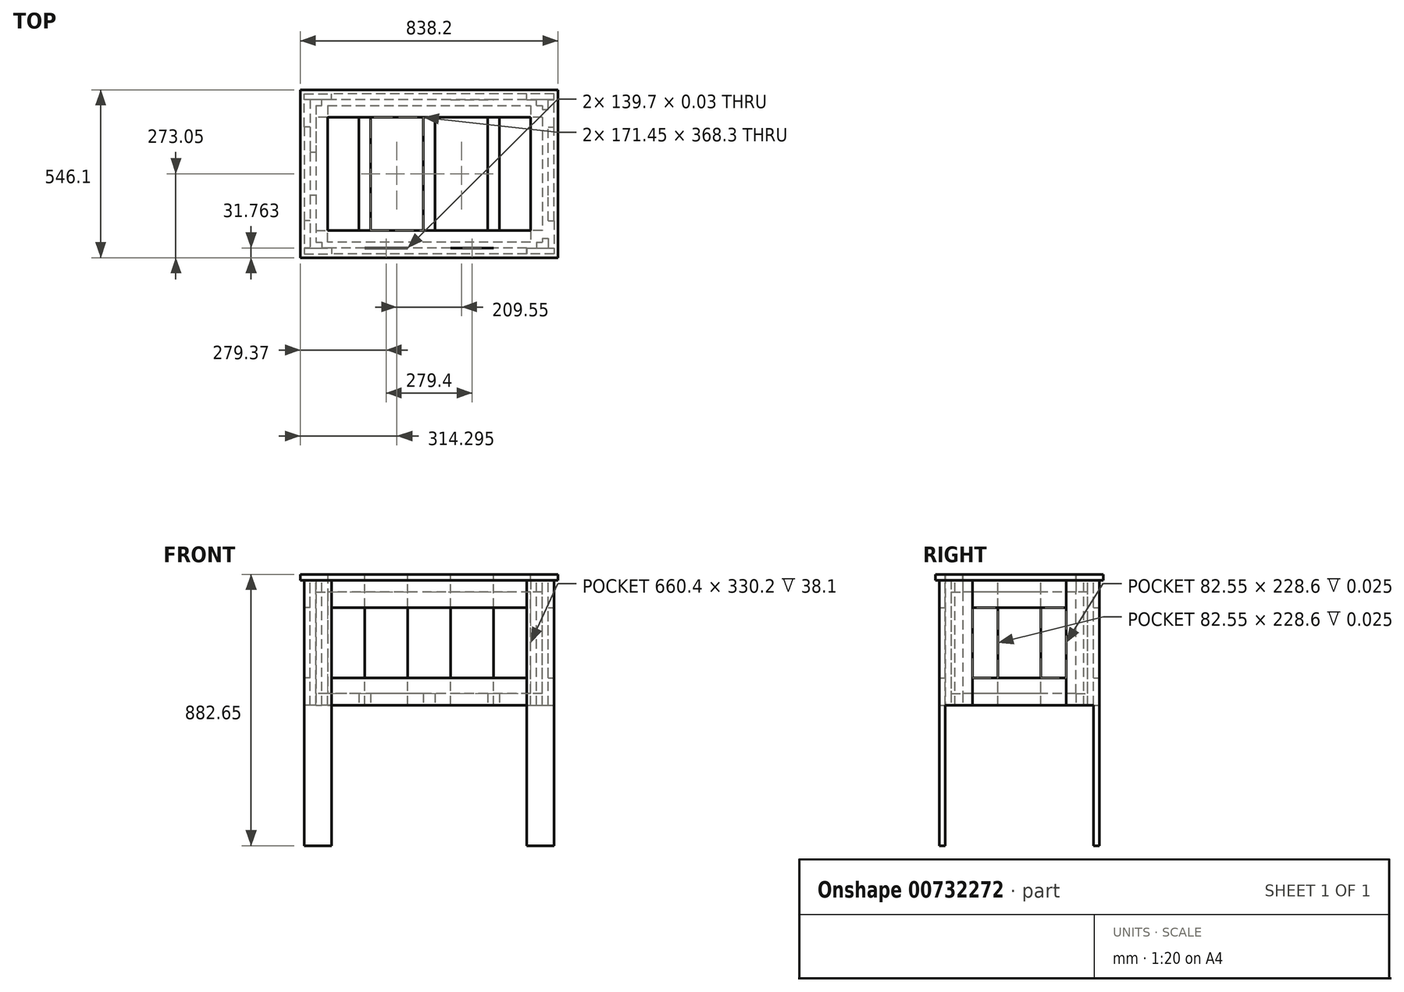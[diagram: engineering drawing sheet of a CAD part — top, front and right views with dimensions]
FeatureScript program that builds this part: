
annotation { "Feature Type Name" : "Feature", "Feature Type Description" : "" }
export const myFeature = defineFeature(function(context is Context, id is Id, definition is map)
    precondition{}
    {
        {
            var Q0;
            Q0=qCreatedBy(makeId("Top.planeOp"),FACE);
            var sketch = newSketch(context, id + "F0", { "sketchPlane" : qUnion([Q0])});
            skLineSegment(sketch, "E0.bottom", {"start": v(0, 0) * mm, "end": v(38.1, 0) * mm});
            skLineSegment(sketch, "E0.top", {"start": v(0, -38.1) * mm, "end": v(38.1, -38.1) * mm});
            skLineSegment(sketch, "E0.left", {"start": v(0, 0) * mm, "end": v(0, -38.1) * mm});
            skLineSegment(sketch, "E0.right", {"start": v(38.1, 0) * mm, "end": v(38.1, -38.1) * mm});
            skSolve(sketch);
        }
        {
            var Q0;
            Q0 = qSketchRegion(id + "F0", true);
            extrude(context, id + "F1", {"entities" : qUnion([Q0]), "depth" : 406.4 * mm, "offsetDistance" : 25.4 * mm});
        }
        {
            var Q0;
            Q0=makeQuery(id+"F1.opExtrude","SWEPT_FACE",FACE,{"disambiguationData":[OSD([sQuery(id+"F0.wireOp",EDGE,"E0.right")])]});
            var sketch = newSketch(context, id + "F2", { "sketchPlane" : qUnion([Q0])});
            skLineSegment(sketch, "E1.bottom", {"start": v(-38.1, 406.4) * mm, "end": v(0, 406.4) * mm});
            skLineSegment(sketch, "E1.top", {"start": v(-38.1, 368.3) * mm, "end": v(0, 368.3) * mm});
            skLineSegment(sketch, "E1.left", {"start": v(-38.1, 406.4) * mm, "end": v(-38.1, 368.3) * mm});
            skLineSegment(sketch, "E1.right", {"start": v(0, 406.4) * mm, "end": v(0, 368.3) * mm});
            skSolve(sketch);
        }
        {
            var Q0;
            Q0=makeQuery(id+"F2.imprint","IMPRINT",FACE,{"disambiguationData":[TD([[makeQuery(id+"F2.imprint","IMPRINT",EDGE,{"derivedFrom":sQuery(id+"F2.wireOp",EDGE,"E1.bottom")}),1.0]])]});
            var sketch = newSketch(context, id + "F3", { "sketchPlane" : qUnion([Q0])});
            skSolve(sketch);
        }
        {
            var Q0;
            Q0=makeQuery(id+"F3.imprint","IMPRINT",FACE,{"disambiguationData":[TD([[makeQuery(id+"F3.imprint","IMPRINT",EDGE,{"derivedFrom":makeQuery(id+"F2.imprint","IMPRINT",EDGE,{"derivedFrom":sQuery(id+"F2.wireOp",EDGE,"E1.bottom")})}),1.0]])]});
            extrude(context, id + "F4", {"entities" : qUnion([Q0]), "operationType" : NewBodyOperationType.ADD, "depth" : 660.4 * mm, "offsetDistance" : 25.4 * mm});
        }
        {
            var Q0;
            Q0=makeQuery(id+"F4.boolean.opBoolean","MERGE",FACE,{"derivedFrom":[makeQuery(id+"F1.opExtrude","CAP_FACE",FACE,{"disambiguationData":[OSD([sQuery(id+"F0.wireOp",EDGE,"E0.bottom"),sQuery(id+"F0.wireOp",EDGE,"E0.top"),sQuery(id+"F0.wireOp",EDGE,"E0.left"),sQuery(id+"F0.wireOp",EDGE,"E0.right")])],"isStart":false}),makeQuery(id+"F4.opExtrude","SWEPT_FACE",FACE,{"disambiguationData":[OSD([sQuery(id+"F2.wireOp",EDGE,"E1.bottom")])]})]});
            var sketch = newSketch(context, id + "F5", { "sketchPlane" : qUnion([Q0])});
            skLineSegment(sketch, "E2.bottom", {"start": v(698.5, 0) * mm, "end": v(736.6, 0) * mm});
            skLineSegment(sketch, "E2.top", {"start": v(698.5, -38.1) * mm, "end": v(736.6, -38.1) * mm});
            skLineSegment(sketch, "E2.left", {"start": v(698.5, 0) * mm, "end": v(698.5, -38.1) * mm});
            skLineSegment(sketch, "E2.right", {"start": v(736.6, 0) * mm, "end": v(736.6, -38.1) * mm});
            skSolve(sketch);
        }
        {
            var Q0;
            Q0=makeQuery(id+"F5.imprint","IMPRINT",FACE,{"disambiguationData":[TD([[makeQuery(id+"F5.imprint","IMPRINT",EDGE,{"derivedFrom":sQuery(id+"F5.wireOp",EDGE,"E2.bottom")}),-1.0]])]});
            extrude(context, id + "F6", {"entities" : qUnion([Q0]), "operationType" : NewBodyOperationType.ADD, "oppositeDirection" : true, "depth" : 406.4 * mm, "offsetDistance" : 25.4 * mm});
        }
        {
            var Q0;
            Q0 = qSketchRegion(id + "F2", true);
            var sketch = newSketch(context, id + "F7", { "sketchPlane" : qUnion([Q0])});
            skLineSegment(sketch, "E3.bottom", {"start": v(-38.1, 0) * mm, "end": v(0, 0) * mm});
            skLineSegment(sketch, "E3.top", {"start": v(-38.1, 38.1) * mm, "end": v(0, 38.1) * mm});
            skLineSegment(sketch, "E3.left", {"start": v(-38.1, 0) * mm, "end": v(-38.1, 38.1) * mm});
            skLineSegment(sketch, "E3.right", {"start": v(0, 0) * mm, "end": v(0, 38.1) * mm});
            skSolve(sketch);
        }
        {
            var Q0;
            Q0=makeQuery(id+"F7.imprint","IMPRINT",FACE,{"disambiguationData":[TD([[makeQuery(id+"F7.imprint","IMPRINT",EDGE,{"derivedFrom":sQuery(id+"F7.wireOp",EDGE,"E3.bottom")}),1.0]])]});
            extrude(context, id + "F8", {"entities" : qUnion([Q0]), "operationType" : NewBodyOperationType.ADD, "endBound" : BoundingType.UP_TO_NEXT, "depth" : 25.4 * mm, "offsetDistance" : 25.4 * mm});
        }
        {
            var Q0;
            Q0=makeQuery(id+"F8.boolean.opBoolean","MERGE",FACE,{"derivedFrom":[makeQuery(id+"F6.boolean.opBoolean","MERGE",FACE,{"derivedFrom":[makeQuery(id+"F4.boolean.opBoolean","MERGE",FACE,{"derivedFrom":[makeQuery(id+"F1.opExtrude","SWEPT_FACE",FACE,{"disambiguationData":[OSD([sQuery(id+"F0.wireOp",EDGE,"E0.bottom")])]}),makeQuery(id+"F4.opExtrude","SWEPT_FACE",FACE,{"disambiguationData":[OSD([sQuery(id+"F2.wireOp",EDGE,"E1.right")])]})]}),makeQuery(id+"F6.opExtrude","SWEPT_FACE",FACE,{"disambiguationData":[OSD([sQuery(id+"F5.wireOp",EDGE,"E2.bottom")])]})]}),makeQuery(id+"F8.opExtrude","SWEPT_FACE",FACE,{"disambiguationData":[OSD([sQuery(id+"F7.wireOp",EDGE,"E3.right")])]})]});
            var sketch = newSketch(context, id + "F9", { "sketchPlane" : qUnion([Q0])});
            skLineSegment(sketch, "E4.bottom", {"start": v(-736.6, 406.4) * mm, "end": v(-698.5, 406.4) * mm});
            skLineSegment(sketch, "E4.top", {"start": v(-736.6, 368.3) * mm, "end": v(-698.5, 368.3) * mm});
            skLineSegment(sketch, "E4.left", {"start": v(-736.6, 406.4) * mm, "end": v(-736.6, 368.3) * mm});
            skLineSegment(sketch, "E4.right", {"start": v(-698.5, 406.4) * mm, "end": v(-698.5, 368.3) * mm});
            skLineSegment(sketch, "E5.bottom", {"start": v(-736.6, 0) * mm, "end": v(-698.5, 0) * mm});
            skLineSegment(sketch, "E5.top", {"start": v(-736.6, 38.1) * mm, "end": v(-698.5, 38.1) * mm});
            skLineSegment(sketch, "E5.left", {"start": v(-736.6, 0) * mm, "end": v(-736.6, 38.1) * mm});
            skLineSegment(sketch, "E5.right", {"start": v(-698.5, 0) * mm, "end": v(-698.5, 38.1) * mm});
            skLineSegment(sketch, "E6.bottom", {"start": v(-698.5, 38.1) * mm, "end": v(-698.5, 38.1) * mm});
            skLineSegment(sketch, "E6.top", {"start": v(-698.5, 38.1) * mm, "end": v(-698.5, 38.1) * mm});
            skLineSegment(sketch, "E6.left", {"start": v(-698.5, 38.1) * mm, "end": v(-698.5, 38.1) * mm});
            skLineSegment(sketch, "E6.right", {"start": v(-698.5, 38.1) * mm, "end": v(-698.5, 38.1) * mm});
            skLineSegment(sketch, "E7.bottom", {"start": v(0, 406.4) * mm, "end": v(-38.1, 406.4) * mm});
            skLineSegment(sketch, "E7.top", {"start": v(0, 368.3) * mm, "end": v(-38.1, 368.3) * mm});
            skLineSegment(sketch, "E7.left", {"start": v(0, 406.4) * mm, "end": v(0, 368.3) * mm});
            skLineSegment(sketch, "E7.right", {"start": v(-38.1, 406.4) * mm, "end": v(-38.1, 368.3) * mm});
            skLineSegment(sketch, "E8.bottom", {"start": v(0, 0) * mm, "end": v(-38.1, 0) * mm});
            skLineSegment(sketch, "E8.top", {"start": v(0, 38.1) * mm, "end": v(-38.1, 38.1) * mm});
            skLineSegment(sketch, "E8.left", {"start": v(0, 0) * mm, "end": v(0, 38.1) * mm});
            skLineSegment(sketch, "E8.right", {"start": v(-38.1, 0) * mm, "end": v(-38.1, 38.1) * mm});
            skSolve(sketch);
        }
        {
            var Q0;
            Q0=makeQuery(id+"F9.imprint","IMPRINT",FACE,{"disambiguationData":[TD([[makeQuery(id+"F9.imprint","IMPRINT",EDGE,{"derivedFrom":sQuery(id+"F9.wireOp",EDGE,"E4.bottom")}),1.0]])]});
            var Q1;
            Q1=makeQuery(id+"F9.imprint","IMPRINT",FACE,{"disambiguationData":[TD([[makeQuery(id+"F9.imprint","IMPRINT",EDGE,{"derivedFrom":sQuery(id+"F9.wireOp",EDGE,"E5.bottom")}),-1.0]])]});
            var Q2;
            Q2=makeQuery(id+"F9.imprint","IMPRINT",FACE,{"disambiguationData":[TD([[makeQuery(id+"F9.imprint","IMPRINT",EDGE,{"derivedFrom":sQuery(id+"F9.wireOp",EDGE,"E8.bottom")}),-1.0]])]});
            var Q3;
            Q3=makeQuery(id+"F9.imprint","IMPRINT",FACE,{"disambiguationData":[TD([[makeQuery(id+"F9.imprint","IMPRINT",EDGE,{"derivedFrom":sQuery(id+"F9.wireOp",EDGE,"E7.bottom")}),1.0]])]});
            extrude(context, id + "F10", {"entities" : qUnion([Q0, Q1, Q2, Q3]), "operationType" : NewBodyOperationType.ADD, "depth" : 368.3 * mm, "offsetDistance" : 25.4 * mm});
        }
        {
            var Q0;
            Q0=makeQuery(id+"F10.boolean.opBoolean","MERGE",FACE,{"derivedFrom":[makeQuery(id+"F6.opExtrude","SWEPT_FACE",FACE,{"disambiguationData":[OSD([sQuery(id+"F5.wireOp",EDGE,"E2.right")])]}),makeQuery(id+"F10.opExtrude","SWEPT_FACE",FACE,{"disambiguationData":[OSD([sQuery(id+"F9.wireOp",EDGE,"E4.left")])]}),makeQuery(id+"F10.opExtrude","SWEPT_FACE",FACE,{"disambiguationData":[OSD([sQuery(id+"F9.wireOp",EDGE,"E5.left")])]})]});
            var sketch = newSketch(context, id + "F11", { "sketchPlane" : qUnion([Q0])});
            skLineSegment(sketch, "E9.bottom", {"start": v(368.3, 406.4) * mm, "end": v(406.4, 406.4) * mm});
            skLineSegment(sketch, "E9.top", {"start": v(368.3, 368.3) * mm, "end": v(406.4, 368.3) * mm});
            skLineSegment(sketch, "E9.left", {"start": v(368.3, 406.4) * mm, "end": v(368.3, 368.3) * mm});
            skLineSegment(sketch, "E9.right", {"start": v(406.4, 406.4) * mm, "end": v(406.4, 368.3) * mm});
            skLineSegment(sketch, "E10.bottom", {"start": v(368.3, 38.1) * mm, "end": v(406.4, 38.1) * mm});
            skLineSegment(sketch, "E10.top", {"start": v(368.3, 0) * mm, "end": v(406.4, 0) * mm});
            skLineSegment(sketch, "E10.left", {"start": v(368.3, 38.1) * mm, "end": v(368.3, 0) * mm});
            skLineSegment(sketch, "E10.right", {"start": v(406.4, 38.1) * mm, "end": v(406.4, 0) * mm});
            skSolve(sketch);
        }
        {
            var Q0;
            Q0 = qSketchRegion(id + "F11", true);
            var Q1;
            Q1=makeQuery(id+"F11.imprint","IMPRINT",FACE,{"disambiguationData":[TD([[makeQuery(id+"F11.imprint","IMPRINT",EDGE,{"derivedFrom":sQuery(id+"F11.wireOp",EDGE,"E9.bottom")}),-1.0]])]});
            var Q2;
            Q2=makeQuery(id+"F11.imprint","IMPRINT",FACE,{"disambiguationData":[TD([[makeQuery(id+"F11.imprint","IMPRINT",EDGE,{"derivedFrom":sQuery(id+"F11.wireOp",EDGE,"E10.bottom")}),-1.0]])]});
            extrude(context, id + "F12", {"entities" : qUnion([Q0, Q1, Q2]), "operationType" : NewBodyOperationType.ADD, "oppositeDirection" : true, "depth" : 736.6 * mm, "offsetDistance" : 25.4 * mm});
        }
        {
            var Q0;
            Q0=makeQuery(id+"F12.boolean.opBoolean","MERGE",FACE,{"derivedFrom":[makeQuery(id+"F10.opExtrude","SWEPT_FACE",FACE,{"disambiguationData":[OSD([sQuery(id+"F9.wireOp",EDGE,"E4.top")])]}),makeQuery(id+"F10.opExtrude","SWEPT_FACE",FACE,{"disambiguationData":[OSD([sQuery(id+"F9.wireOp",EDGE,"E7.top")])]}),makeQuery(id+"F12.opExtrude","SWEPT_FACE",FACE,{"disambiguationData":[OSD([sQuery(id+"F11.wireOp",EDGE,"E9.top")])]})]});
            var sketch = newSketch(context, id + "F13", { "sketchPlane" : qUnion([Q0])});
            skLineSegment(sketch, "E11.bottom", {"start": v(736.6, -406.4) * mm, "end": v(698.5, -406.4) * mm});
            skLineSegment(sketch, "E11.top", {"start": v(736.6, -368.3) * mm, "end": v(698.5, -368.3) * mm});
            skLineSegment(sketch, "E11.left", {"start": v(736.6, -406.4) * mm, "end": v(736.6, -368.3) * mm});
            skLineSegment(sketch, "E11.right", {"start": v(698.5, -406.4) * mm, "end": v(698.5, -368.3) * mm});
            skLineSegment(sketch, "E12.bottom", {"start": v(0, -406.4) * mm, "end": v(38.1, -406.4) * mm});
            skLineSegment(sketch, "E12.top", {"start": v(0, -368.3) * mm, "end": v(38.1, -368.3) * mm});
            skLineSegment(sketch, "E12.left", {"start": v(0, -406.4) * mm, "end": v(0, -368.3) * mm});
            skLineSegment(sketch, "E12.right", {"start": v(38.1, -406.4) * mm, "end": v(38.1, -368.3) * mm});
            skSolve(sketch);
        }
        {
            var Q0;
            Q0=makeQuery(id+"F13.imprint","IMPRINT",FACE,{"disambiguationData":[TD([[makeQuery(id+"F13.imprint","IMPRINT",EDGE,{"derivedFrom":sQuery(id+"F13.wireOp",EDGE,"E11.bottom")}),1.0]])]});
            var Q1;
            Q1 = qSketchRegion(id + "F13", true);
            var Q2;
            Q2=makeQuery(id+"F13.imprint","IMPRINT",FACE,{"disambiguationData":[TD([[makeQuery(id+"F13.imprint","IMPRINT",EDGE,{"derivedFrom":sQuery(id+"F13.wireOp",EDGE,"E12.bottom")}),1.0]])]});
            extrude(context, id + "F14", {"entities" : qUnion([Q0, Q1, Q2]), "operationType" : NewBodyOperationType.ADD, "endBound" : BoundingType.UP_TO_NEXT, "depth" : 25.4 * mm, "offsetDistance" : 25.4 * mm});
        }
        {
            var Q0;
            {var subQ0=makeQuery(id+"F8.opExtrude","SWEPT_FACE",FACE,{"disambiguationData":[OSD([sQuery(id+"F7.wireOp",EDGE,"E3.right")])]});var subQ3=sQuery(id+"F0.wireOp",EDGE,"E0.bottom");var subQ4=makeQuery(id+"F1.opExtrude","SWEPT_FACE",FACE,{"disambiguationData":[OSD([subQ3])]});var subQ5=sQuery(id+"F5.wireOp",EDGE,"E2.bottom");var subQ6=makeQuery(id+"F6.opExtrude","SWEPT_FACE",FACE,{"disambiguationData":[OSD([subQ5])]});var subQ7=makeQuery(id+"F4.opExtrude","SWEPT_FACE",FACE,{"disambiguationData":[OSD([sQuery(id+"F2.wireOp",EDGE,"E1.right")])]});Q0=makeQuery(id+"F10.boolean.opBoolean","SPLIT",FACE,{"disambiguationData":[TD([makeQuery(id+"F8.opExtrude","SWEPT_FACE",FACE,{"disambiguationData":[OSD([sQuery(id+"F7.wireOp",EDGE,"E3.bottom")])]})])],"derivedFrom":makeQuery(id+"F8.boolean.opBoolean","MERGE",FACE,{"derivedFrom":[makeQuery(id+"F6.boolean.opBoolean","MERGE",FACE,{"derivedFrom":[makeQuery(id+"F4.boolean.opBoolean","MERGE",FACE,{"derivedFrom":[subQ4,subQ7]}),subQ6]}),subQ0]})});}
            var sketch = newSketch(context, id + "F15", { "sketchPlane" : qUnion([Q0])});
            skLineSegment(sketch, "E13.bottom", {"start": v(-596.9, 38.1) * mm, "end": v(-558.8, 38.1) * mm});
            skLineSegment(sketch, "E13.top", {"start": v(-596.9, 0) * mm, "end": v(-558.8, 0) * mm});
            skLineSegment(sketch, "E13.left", {"start": v(-596.9, 38.1) * mm, "end": v(-596.9, 0) * mm});
            skLineSegment(sketch, "E13.right", {"start": v(-558.8, 38.1) * mm, "end": v(-558.8, 0) * mm});
            skLineSegment(sketch, "E14.bottom", {"start": v(-387.35, 38.1) * mm, "end": v(-349.25, 38.1) * mm});
            skLineSegment(sketch, "E14.top", {"start": v(-387.35, -0.88) * mm, "end": v(-349.25, -0.88) * mm});
            skLineSegment(sketch, "E14.left", {"start": v(-387.35, 38.1) * mm, "end": v(-387.35, -0.88) * mm});
            skLineSegment(sketch, "E14.right", {"start": v(-349.25, 38.1) * mm, "end": v(-349.25, -0.88) * mm});
            skLineSegment(sketch, "E15.bottom", {"start": v(-177.8, 38.1) * mm, "end": v(-139.7, 38.1) * mm});
            skLineSegment(sketch, "E15.top", {"start": v(-177.8, 0) * mm, "end": v(-139.7, 0) * mm});
            skLineSegment(sketch, "E15.left", {"start": v(-177.8, 38.1) * mm, "end": v(-177.8, 0) * mm});
            skLineSegment(sketch, "E15.right", {"start": v(-139.7, 38.1) * mm, "end": v(-139.7, 0) * mm});
            skSolve(sketch);
        }
        {
            var Q0;
            Q0=makeQuery(id+"F15.imprint","IMPRINT",FACE,{"disambiguationData":[TD([[makeQuery(id+"F15.imprint","IMPRINT",EDGE,{"derivedFrom":sQuery(id+"F15.wireOp",EDGE,"E13.bottom")}),-1.0]])]});
            var Q1;
            {var subQ0=sQuery(id+"F15.wireOp",EDGE,"E14.bottom");Q1=makeQuery(id+"F15.imprint","IMPRINT",FACE,{"disambiguationData":[TD([[makeQuery(id+"F15.imprint","IMPRINT",EDGE,{"derivedFrom":subQ0}),-1.0]])]});}
            var Q2;
            Q2=makeQuery(id+"F15.imprint","IMPRINT",FACE,{"disambiguationData":[TD([[makeQuery(id+"F15.imprint","IMPRINT",EDGE,{"derivedFrom":sQuery(id+"F15.wireOp",EDGE,"E15.bottom")}),-1.0]])]});
            extrude(context, id + "F16", {"entities" : qUnion([Q0, Q1, Q2]), "operationType" : NewBodyOperationType.ADD, "endBound" : BoundingType.UP_TO_NEXT, "depth" : 25.4 * mm, "offsetDistance" : 25.4 * mm});
        }
        {
            var Q0;
            Q0=makeQuery(id+"F12.boolean.opBoolean","MERGE",FACE,{"derivedFrom":[makeQuery(id+"F10.boolean.opBoolean","MERGE",FACE,{"derivedFrom":[makeQuery(id+"F6.boolean.opBoolean","MERGE",FACE,{"derivedFrom":[makeQuery(id+"F4.boolean.opBoolean","MERGE",FACE,{"derivedFrom":[makeQuery(id+"F1.opExtrude","CAP_FACE",FACE,{"disambiguationData":[OSD([sQuery(id+"F0.wireOp",EDGE,"E0.bottom"),sQuery(id+"F0.wireOp",EDGE,"E0.top"),sQuery(id+"F0.wireOp",EDGE,"E0.left"),sQuery(id+"F0.wireOp",EDGE,"E0.right")])],"isStart":false}),makeQuery(id+"F4.opExtrude","SWEPT_FACE",FACE,{"disambiguationData":[OSD([sQuery(id+"F2.wireOp",EDGE,"E1.bottom")])]})]}),makeQuery(id+"F6.opExtrude","CAP_FACE",FACE,{"disambiguationData":[OSD([sQuery(id+"F5.wireOp",EDGE,"E2.bottom"),sQuery(id+"F5.wireOp",EDGE,"E2.top"),sQuery(id+"F5.wireOp",EDGE,"E2.left"),sQuery(id+"F5.wireOp",EDGE,"E2.right")])],"isStart":true})]}),makeQuery(id+"F10.opExtrude","SWEPT_FACE",FACE,{"disambiguationData":[OSD([sQuery(id+"F9.wireOp",EDGE,"E4.bottom")])]}),makeQuery(id+"F10.opExtrude","SWEPT_FACE",FACE,{"disambiguationData":[OSD([sQuery(id+"F9.wireOp",EDGE,"E7.bottom")])]})]}),makeQuery(id+"F12.opExtrude","SWEPT_FACE",FACE,{"disambiguationData":[OSD([sQuery(id+"F11.wireOp",EDGE,"E9.bottom")])]})]});
            var sketch = newSketch(context, id + "F17", { "sketchPlane" : qUnion([Q0])});
            skLineSegment(sketch, "E16.bottom", {"start": v(298.45, -38.1) * mm, "end": v(438.15, -38.1) * mm});
            skLineSegment(sketch, "E16.top", {"start": v(298.45, -57.15) * mm, "end": v(438.15, -57.15) * mm});
            skLineSegment(sketch, "E16.left", {"start": v(298.45, -38.1) * mm, "end": v(298.45, -57.15) * mm});
            skLineSegment(sketch, "E16.right", {"start": v(438.15, -38.1) * mm, "end": v(438.15, -57.15) * mm});
            skSolve(sketch);
        }
        {
            var Q0;
            Q0=makeQuery(id+"F17.imprint","IMPRINT",FACE,{"disambiguationData":[TD([[makeQuery(id+"F17.imprint","IMPRINT",EDGE,{"derivedFrom":sQuery(id+"F17.wireOp",EDGE,"E16.bottom")}),-1.0]])]});
            extrude(context, id + "F18", {"entities" : qUnion([Q0]), "operationType" : NewBodyOperationType.ADD, "oppositeDirection" : true, "depth" : 406.4 * mm, "offsetDistance" : 25.4 * mm});
        }
        {
            var Q0;
            Q0=makeQuery(id+"F18.boolean.opBoolean","MERGE",FACE,{"derivedFrom":[makeQuery(id+"F12.boolean.opBoolean","MERGE",FACE,{"derivedFrom":[makeQuery(id+"F10.boolean.opBoolean","MERGE",FACE,{"derivedFrom":[makeQuery(id+"F6.boolean.opBoolean","MERGE",FACE,{"derivedFrom":[makeQuery(id+"F4.boolean.opBoolean","MERGE",FACE,{"derivedFrom":[makeQuery(id+"F1.opExtrude","CAP_FACE",FACE,{"disambiguationData":[OSD([sQuery(id+"F0.wireOp",EDGE,"E0.bottom"),sQuery(id+"F0.wireOp",EDGE,"E0.top"),sQuery(id+"F0.wireOp",EDGE,"E0.left"),sQuery(id+"F0.wireOp",EDGE,"E0.right")])],"isStart":false}),makeQuery(id+"F4.opExtrude","SWEPT_FACE",FACE,{"disambiguationData":[OSD([sQuery(id+"F2.wireOp",EDGE,"E1.bottom")])]})]}),makeQuery(id+"F6.opExtrude","CAP_FACE",FACE,{"disambiguationData":[OSD([sQuery(id+"F5.wireOp",EDGE,"E2.bottom"),sQuery(id+"F5.wireOp",EDGE,"E2.top"),sQuery(id+"F5.wireOp",EDGE,"E2.left"),sQuery(id+"F5.wireOp",EDGE,"E2.right")])],"isStart":true})]}),makeQuery(id+"F10.opExtrude","SWEPT_FACE",FACE,{"disambiguationData":[OSD([sQuery(id+"F9.wireOp",EDGE,"E4.bottom")])]}),makeQuery(id+"F10.opExtrude","SWEPT_FACE",FACE,{"disambiguationData":[OSD([sQuery(id+"F9.wireOp",EDGE,"E7.bottom")])]})]}),makeQuery(id+"F12.opExtrude","SWEPT_FACE",FACE,{"disambiguationData":[OSD([sQuery(id+"F11.wireOp",EDGE,"E9.bottom")])]})]}),makeQuery(id+"F18.opExtrude","CAP_FACE",FACE,{"disambiguationData":[OSD([sQuery(id+"F17.wireOp",EDGE,"E16.bottom"),sQuery(id+"F17.wireOp",EDGE,"E16.top"),sQuery(id+"F17.wireOp",EDGE,"E16.left"),sQuery(id+"F17.wireOp",EDGE,"E16.right")])],"isStart":true})]});
            var sketch = newSketch(context, id + "F19", { "sketchPlane" : qUnion([Q0])});
            skLineSegment(sketch, "E17.bottom", {"start": v(158.75, -38.1) * mm, "end": v(298.45, -38.1) * mm});
            skLineSegment(sketch, "E17.top", {"start": v(158.75, -57.12) * mm, "end": v(298.45, -57.12) * mm});
            skLineSegment(sketch, "E17.left", {"start": v(158.75, -38.1) * mm, "end": v(158.75, -57.12) * mm});
            skLineSegment(sketch, "E17.right", {"start": v(298.45, -38.1) * mm, "end": v(298.45, -57.12) * mm});
            skSolve(sketch);
        }
        {
            var Q0;
            Q0=makeQuery(id+"F19.imprint","IMPRINT",FACE,{"disambiguationData":[TD([[makeQuery(id+"F19.imprint","IMPRINT",EDGE,{"derivedFrom":sQuery(id+"F19.wireOp",EDGE,"E17.bottom")}),-1.0]])]});
            extrude(context, id + "F20", {"entities" : qUnion([Q0]), "operationType" : NewBodyOperationType.ADD, "oppositeDirection" : true, "depth" : 406.4 * mm, "offsetDistance" : 25.4 * mm});
        }
        {
            var Q0;
            Q0 = qSketchRegion(id + "F0", true);
            var sketch = newSketch(context, id + "F21", { "sketchPlane" : qUnion([Q0])});
            skLineSegment(sketch, "E18.bottom", {"start": v(438.15, -38.1) * mm, "end": v(577.85, -38.1) * mm});
            skLineSegment(sketch, "E18.top", {"start": v(438.15, -57.12) * mm, "end": v(577.85, -57.12) * mm});
            skLineSegment(sketch, "E18.left", {"start": v(438.15, -38.1) * mm, "end": v(438.15, -57.12) * mm});
            skLineSegment(sketch, "E18.right", {"start": v(577.85, -38.1) * mm, "end": v(577.85, -57.12) * mm});
            skSolve(sketch);
        }
        {
            var Q0;
            Q0=makeQuery(id+"F21.imprint","IMPRINT",FACE,{"disambiguationData":[TD([[makeQuery(id+"F21.imprint","IMPRINT",EDGE,{"derivedFrom":sQuery(id+"F21.wireOp",EDGE,"E18.bottom")}),-1.0]])]});
            extrude(context, id + "F22", {"entities" : qUnion([Q0]), "operationType" : NewBodyOperationType.ADD, "depth" : 406.4 * mm, "offsetDistance" : 25.4 * mm});
        }
        {
            var Q0;
            Q0=makeQuery(id+"F22.boolean.opBoolean","MERGE",FACE,{"derivedFrom":[makeQuery(id+"F20.boolean.opBoolean","MERGE",FACE,{"derivedFrom":[makeQuery(id+"F18.boolean.opBoolean","MERGE",FACE,{"derivedFrom":[makeQuery(id+"F12.boolean.opBoolean","MERGE",FACE,{"derivedFrom":[makeQuery(id+"F10.boolean.opBoolean","MERGE",FACE,{"derivedFrom":[makeQuery(id+"F6.boolean.opBoolean","MERGE",FACE,{"derivedFrom":[makeQuery(id+"F4.boolean.opBoolean","MERGE",FACE,{"derivedFrom":[makeQuery(id+"F1.opExtrude","CAP_FACE",FACE,{"disambiguationData":[OSD([sQuery(id+"F0.wireOp",EDGE,"E0.bottom"),sQuery(id+"F0.wireOp",EDGE,"E0.top"),sQuery(id+"F0.wireOp",EDGE,"E0.left"),sQuery(id+"F0.wireOp",EDGE,"E0.right")])],"isStart":false}),makeQuery(id+"F4.opExtrude","SWEPT_FACE",FACE,{"disambiguationData":[OSD([sQuery(id+"F2.wireOp",EDGE,"E1.bottom")])]})]}),makeQuery(id+"F6.opExtrude","CAP_FACE",FACE,{"disambiguationData":[OSD([sQuery(id+"F5.wireOp",EDGE,"E2.bottom"),sQuery(id+"F5.wireOp",EDGE,"E2.top"),sQuery(id+"F5.wireOp",EDGE,"E2.left"),sQuery(id+"F5.wireOp",EDGE,"E2.right")])],"isStart":true})]}),makeQuery(id+"F10.opExtrude","SWEPT_FACE",FACE,{"disambiguationData":[OSD([sQuery(id+"F9.wireOp",EDGE,"E4.bottom")])]}),makeQuery(id+"F10.opExtrude","SWEPT_FACE",FACE,{"disambiguationData":[OSD([sQuery(id+"F9.wireOp",EDGE,"E7.bottom")])]})]}),makeQuery(id+"F12.opExtrude","SWEPT_FACE",FACE,{"disambiguationData":[OSD([sQuery(id+"F11.wireOp",EDGE,"E9.bottom")])]})]}),makeQuery(id+"F18.opExtrude","CAP_FACE",FACE,{"disambiguationData":[OSD([sQuery(id+"F17.wireOp",EDGE,"E16.bottom"),sQuery(id+"F17.wireOp",EDGE,"E16.top"),sQuery(id+"F17.wireOp",EDGE,"E16.left"),sQuery(id+"F17.wireOp",EDGE,"E16.right")])],"isStart":true})]}),makeQuery(id+"F20.opExtrude","CAP_FACE",FACE,{"disambiguationData":[OSD([sQuery(id+"F19.wireOp",EDGE,"E17.bottom"),sQuery(id+"F19.wireOp",EDGE,"E17.top"),sQuery(id+"F19.wireOp",EDGE,"E17.left"),sQuery(id+"F19.wireOp",EDGE,"E17.right")])],"isStart":true})]}),makeQuery(id+"F22.opExtrude","CAP_FACE",FACE,{"disambiguationData":[OSD([sQuery(id+"F21.wireOp",EDGE,"E18.bottom"),sQuery(id+"F21.wireOp",EDGE,"E18.top"),sQuery(id+"F21.wireOp",EDGE,"E18.left"),sQuery(id+"F21.wireOp",EDGE,"E18.right")])],"isStart":false})]});
            var sketch = newSketch(context, id + "F23", { "sketchPlane" : qUnion([Q0])});
            skLineSegment(sketch, "E19.bottom", {"start": v(577.85, -38.1) * mm, "end": v(717.55, -38.1) * mm});
            skLineSegment(sketch, "E19.top", {"start": v(577.85, -57.15) * mm, "end": v(717.55, -57.15) * mm});
            skLineSegment(sketch, "E19.left", {"start": v(577.85, -38.1) * mm, "end": v(577.85, -57.15) * mm});
            skLineSegment(sketch, "E19.right", {"start": v(717.55, -38.1) * mm, "end": v(717.55, -57.15) * mm});
            skLineSegment(sketch, "E20.bottom", {"start": v(158.75, -38.1) * mm, "end": v(19.05, -38.1) * mm});
            skLineSegment(sketch, "E20.top", {"start": v(158.75, -57.15) * mm, "end": v(19.05, -57.15) * mm});
            skLineSegment(sketch, "E20.left", {"start": v(158.75, -38.1) * mm, "end": v(158.75, -57.15) * mm});
            skLineSegment(sketch, "E20.right", {"start": v(19.05, -38.1) * mm, "end": v(19.05, -57.15) * mm});
            skSolve(sketch);
        }
        {
            var Q0;
            {var subQ3=sQuery(id+"F23.wireOp",EDGE,"E20.bottom");Q0=makeQuery(id+"F23.imprint","IMPRINT",FACE,{"disambiguationData":[TD([[makeQuery(id+"F23.imprint","IMPRINT",EDGE,{"derivedFrom":subQ3}),-1.0]])]});}
            var Q1;
            {var subQ3=sQuery(id+"F23.wireOp",EDGE,"E19.bottom");Q1=makeQuery(id+"F23.imprint","IMPRINT",FACE,{"disambiguationData":[TD([[makeQuery(id+"F23.imprint","IMPRINT",EDGE,{"derivedFrom":subQ3}),-1.0]])]});}
            extrude(context, id + "F24", {"entities" : qUnion([Q0, Q1]), "operationType" : NewBodyOperationType.ADD, "oppositeDirection" : true, "depth" : 406.4 * mm, "offsetDistance" : 25.4 * mm});
        }
        {
            var Q0;
            Q0=makeQuery(id+"F24.boolean.opBoolean","MERGE",FACE,{"derivedFrom":[makeQuery(id+"F22.boolean.opBoolean","MERGE",FACE,{"derivedFrom":[makeQuery(id+"F20.boolean.opBoolean","MERGE",FACE,{"derivedFrom":[makeQuery(id+"F18.boolean.opBoolean","MERGE",FACE,{"derivedFrom":[makeQuery(id+"F12.boolean.opBoolean","MERGE",FACE,{"derivedFrom":[makeQuery(id+"F10.boolean.opBoolean","MERGE",FACE,{"derivedFrom":[makeQuery(id+"F6.boolean.opBoolean","MERGE",FACE,{"derivedFrom":[makeQuery(id+"F4.boolean.opBoolean","MERGE",FACE,{"derivedFrom":[makeQuery(id+"F1.opExtrude","CAP_FACE",FACE,{"disambiguationData":[OSD([sQuery(id+"F0.wireOp",EDGE,"E0.bottom"),sQuery(id+"F0.wireOp",EDGE,"E0.top"),sQuery(id+"F0.wireOp",EDGE,"E0.left"),sQuery(id+"F0.wireOp",EDGE,"E0.right")])],"isStart":false}),makeQuery(id+"F4.opExtrude","SWEPT_FACE",FACE,{"disambiguationData":[OSD([sQuery(id+"F2.wireOp",EDGE,"E1.bottom")])]})]}),makeQuery(id+"F6.opExtrude","CAP_FACE",FACE,{"disambiguationData":[OSD([sQuery(id+"F5.wireOp",EDGE,"E2.bottom"),sQuery(id+"F5.wireOp",EDGE,"E2.top"),sQuery(id+"F5.wireOp",EDGE,"E2.left"),sQuery(id+"F5.wireOp",EDGE,"E2.right")])],"isStart":true})]}),makeQuery(id+"F10.opExtrude","SWEPT_FACE",FACE,{"disambiguationData":[OSD([sQuery(id+"F9.wireOp",EDGE,"E4.bottom")])]}),makeQuery(id+"F10.opExtrude","SWEPT_FACE",FACE,{"disambiguationData":[OSD([sQuery(id+"F9.wireOp",EDGE,"E7.bottom")])]})]}),makeQuery(id+"F12.opExtrude","SWEPT_FACE",FACE,{"disambiguationData":[OSD([sQuery(id+"F11.wireOp",EDGE,"E9.bottom")])]})]}),makeQuery(id+"F18.opExtrude","CAP_FACE",FACE,{"disambiguationData":[OSD([sQuery(id+"F17.wireOp",EDGE,"E16.bottom"),sQuery(id+"F17.wireOp",EDGE,"E16.top"),sQuery(id+"F17.wireOp",EDGE,"E16.left"),sQuery(id+"F17.wireOp",EDGE,"E16.right")])],"isStart":true})]}),makeQuery(id+"F20.opExtrude","CAP_FACE",FACE,{"disambiguationData":[OSD([sQuery(id+"F19.wireOp",EDGE,"E17.bottom"),sQuery(id+"F19.wireOp",EDGE,"E17.top"),sQuery(id+"F19.wireOp",EDGE,"E17.left"),sQuery(id+"F19.wireOp",EDGE,"E17.right")])],"isStart":true})]}),makeQuery(id+"F22.opExtrude","CAP_FACE",FACE,{"disambiguationData":[OSD([sQuery(id+"F21.wireOp",EDGE,"E18.bottom"),sQuery(id+"F21.wireOp",EDGE,"E18.top"),sQuery(id+"F21.wireOp",EDGE,"E18.left"),sQuery(id+"F21.wireOp",EDGE,"E18.right")])],"isStart":false})]}),makeQuery(id+"F24.opExtrude","CAP_FACE",FACE,{"disambiguationData":[OSD([sQuery(id+"F23.wireOp",EDGE,"E19.bottom"),sQuery(id+"F23.wireOp",EDGE,"E19.top"),sQuery(id+"F23.wireOp",EDGE,"E19.left"),sQuery(id+"F23.wireOp",EDGE,"E19.right")])],"isStart":true}),makeQuery(id+"F24.opExtrude","CAP_FACE",FACE,{"disambiguationData":[OSD([sQuery(id+"F23.wireOp",EDGE,"E20.bottom"),sQuery(id+"F23.wireOp",EDGE,"E20.top"),sQuery(id+"F23.wireOp",EDGE,"E20.left"),sQuery(id+"F23.wireOp",EDGE,"E20.right")])],"isStart":true})]});
            var sketch = newSketch(context, id + "F25", { "sketchPlane" : qUnion([Q0])});
            skLineSegment(sketch, "E21.bottom", {"start": v(736.6, 254) * mm, "end": v(755.65, 254) * mm});
            skLineSegment(sketch, "E21.top", {"start": v(736.6, 114.3) * mm, "end": v(755.65, 114.3) * mm});
            skLineSegment(sketch, "E21.left", {"start": v(736.6, 254) * mm, "end": v(736.6, 114.3) * mm});
            skLineSegment(sketch, "E21.right", {"start": v(755.65, 254) * mm, "end": v(755.65, 114.3) * mm});
            skSolve(sketch);
        }
        {
            var Q0;
            Q0=makeQuery(id+"F25.imprint","IMPRINT",FACE,{"disambiguationData":[TD([[makeQuery(id+"F25.imprint","IMPRINT",EDGE,{"derivedFrom":sQuery(id+"F25.wireOp",EDGE,"E21.bottom")}),-1.0]])]});
            extrude(context, id + "F26", {"entities" : qUnion([Q0]), "operationType" : NewBodyOperationType.ADD, "oppositeDirection" : true, "depth" : 406.4 * mm, "offsetDistance" : 25.4 * mm});
        }
        {
            var Q0;
            Q0=makeQuery(id+"F26.boolean.opBoolean","MERGE",FACE,{"derivedFrom":[makeQuery(id+"F24.boolean.opBoolean","MERGE",FACE,{"derivedFrom":[makeQuery(id+"F22.boolean.opBoolean","MERGE",FACE,{"derivedFrom":[makeQuery(id+"F20.boolean.opBoolean","MERGE",FACE,{"derivedFrom":[makeQuery(id+"F18.boolean.opBoolean","MERGE",FACE,{"derivedFrom":[makeQuery(id+"F12.boolean.opBoolean","MERGE",FACE,{"derivedFrom":[makeQuery(id+"F10.boolean.opBoolean","MERGE",FACE,{"derivedFrom":[makeQuery(id+"F6.boolean.opBoolean","MERGE",FACE,{"derivedFrom":[makeQuery(id+"F4.boolean.opBoolean","MERGE",FACE,{"derivedFrom":[makeQuery(id+"F1.opExtrude","CAP_FACE",FACE,{"disambiguationData":[OSD([sQuery(id+"F0.wireOp",EDGE,"E0.bottom"),sQuery(id+"F0.wireOp",EDGE,"E0.top"),sQuery(id+"F0.wireOp",EDGE,"E0.left"),sQuery(id+"F0.wireOp",EDGE,"E0.right")])],"isStart":false}),makeQuery(id+"F4.opExtrude","SWEPT_FACE",FACE,{"disambiguationData":[OSD([sQuery(id+"F2.wireOp",EDGE,"E1.bottom")])]})]}),makeQuery(id+"F6.opExtrude","CAP_FACE",FACE,{"disambiguationData":[OSD([sQuery(id+"F5.wireOp",EDGE,"E2.bottom"),sQuery(id+"F5.wireOp",EDGE,"E2.top"),sQuery(id+"F5.wireOp",EDGE,"E2.left"),sQuery(id+"F5.wireOp",EDGE,"E2.right")])],"isStart":true})]}),makeQuery(id+"F10.opExtrude","SWEPT_FACE",FACE,{"disambiguationData":[OSD([sQuery(id+"F9.wireOp",EDGE,"E4.bottom")])]}),makeQuery(id+"F10.opExtrude","SWEPT_FACE",FACE,{"disambiguationData":[OSD([sQuery(id+"F9.wireOp",EDGE,"E7.bottom")])]})]}),makeQuery(id+"F12.opExtrude","SWEPT_FACE",FACE,{"disambiguationData":[OSD([sQuery(id+"F11.wireOp",EDGE,"E9.bottom")])]})]}),makeQuery(id+"F18.opExtrude","CAP_FACE",FACE,{"disambiguationData":[OSD([sQuery(id+"F17.wireOp",EDGE,"E16.bottom"),sQuery(id+"F17.wireOp",EDGE,"E16.top"),sQuery(id+"F17.wireOp",EDGE,"E16.left"),sQuery(id+"F17.wireOp",EDGE,"E16.right")])],"isStart":true})]}),makeQuery(id+"F20.opExtrude","CAP_FACE",FACE,{"disambiguationData":[OSD([sQuery(id+"F19.wireOp",EDGE,"E17.bottom"),sQuery(id+"F19.wireOp",EDGE,"E17.top"),sQuery(id+"F19.wireOp",EDGE,"E17.left"),sQuery(id+"F19.wireOp",EDGE,"E17.right")])],"isStart":true})]}),makeQuery(id+"F22.opExtrude","CAP_FACE",FACE,{"disambiguationData":[OSD([sQuery(id+"F21.wireOp",EDGE,"E18.bottom"),sQuery(id+"F21.wireOp",EDGE,"E18.top"),sQuery(id+"F21.wireOp",EDGE,"E18.left"),sQuery(id+"F21.wireOp",EDGE,"E18.right")])],"isStart":false})]}),makeQuery(id+"F24.opExtrude","CAP_FACE",FACE,{"disambiguationData":[OSD([sQuery(id+"F23.wireOp",EDGE,"E19.bottom"),sQuery(id+"F23.wireOp",EDGE,"E19.top"),sQuery(id+"F23.wireOp",EDGE,"E19.left"),sQuery(id+"F23.wireOp",EDGE,"E19.right")])],"isStart":true}),makeQuery(id+"F24.opExtrude","CAP_FACE",FACE,{"disambiguationData":[OSD([sQuery(id+"F23.wireOp",EDGE,"E20.bottom"),sQuery(id+"F23.wireOp",EDGE,"E20.top"),sQuery(id+"F23.wireOp",EDGE,"E20.left"),sQuery(id+"F23.wireOp",EDGE,"E20.right")])],"isStart":true})]}),makeQuery(id+"F26.opExtrude","CAP_FACE",FACE,{"disambiguationData":[OSD([sQuery(id+"F25.wireOp",EDGE,"E21.bottom"),sQuery(id+"F25.wireOp",EDGE,"E21.top"),sQuery(id+"F25.wireOp",EDGE,"E21.left"),sQuery(id+"F25.wireOp",EDGE,"E21.right")])],"isStart":true})]});
            var sketch = newSketch(context, id + "F27", { "sketchPlane" : qUnion([Q0])});
            skLineSegment(sketch, "E22.bottom", {"start": v(736.6, 114.3) * mm, "end": v(755.62, 114.3) * mm});
            skLineSegment(sketch, "E22.top", {"start": v(736.6, -25.4) * mm, "end": v(755.62, -25.4) * mm});
            skLineSegment(sketch, "E22.left", {"start": v(736.6, 114.3) * mm, "end": v(736.6, -25.4) * mm});
            skLineSegment(sketch, "E22.right", {"start": v(755.62, 114.3) * mm, "end": v(755.62, -25.4) * mm});
            skSolve(sketch);
        }
        {
            var Q0;
            Q0=makeQuery(id+"F27.imprint","IMPRINT",FACE,{"disambiguationData":[TD([[makeQuery(id+"F27.imprint","IMPRINT",EDGE,{"derivedFrom":sQuery(id+"F27.wireOp",EDGE,"E22.bottom")}),-1.0]])]});
            extrude(context, id + "F28", {"entities" : qUnion([Q0]), "operationType" : NewBodyOperationType.ADD, "oppositeDirection" : true, "depth" : 406.4 * mm, "offsetDistance" : 25.4 * mm});
        }
        {
            var Q0;
            Q0=makeQuery(id+"F28.boolean.opBoolean","MERGE",FACE,{"derivedFrom":[makeQuery(id+"F26.boolean.opBoolean","MERGE",FACE,{"derivedFrom":[makeQuery(id+"F24.boolean.opBoolean","MERGE",FACE,{"derivedFrom":[makeQuery(id+"F22.boolean.opBoolean","MERGE",FACE,{"derivedFrom":[makeQuery(id+"F20.boolean.opBoolean","MERGE",FACE,{"derivedFrom":[makeQuery(id+"F18.boolean.opBoolean","MERGE",FACE,{"derivedFrom":[makeQuery(id+"F12.boolean.opBoolean","MERGE",FACE,{"derivedFrom":[makeQuery(id+"F10.boolean.opBoolean","MERGE",FACE,{"derivedFrom":[makeQuery(id+"F6.boolean.opBoolean","MERGE",FACE,{"derivedFrom":[makeQuery(id+"F4.boolean.opBoolean","MERGE",FACE,{"derivedFrom":[makeQuery(id+"F1.opExtrude","CAP_FACE",FACE,{"disambiguationData":[OSD([sQuery(id+"F0.wireOp",EDGE,"E0.bottom"),sQuery(id+"F0.wireOp",EDGE,"E0.top"),sQuery(id+"F0.wireOp",EDGE,"E0.left"),sQuery(id+"F0.wireOp",EDGE,"E0.right")])],"isStart":false}),makeQuery(id+"F4.opExtrude","SWEPT_FACE",FACE,{"disambiguationData":[OSD([sQuery(id+"F2.wireOp",EDGE,"E1.bottom")])]})]}),makeQuery(id+"F6.opExtrude","CAP_FACE",FACE,{"disambiguationData":[OSD([sQuery(id+"F5.wireOp",EDGE,"E2.bottom"),sQuery(id+"F5.wireOp",EDGE,"E2.top"),sQuery(id+"F5.wireOp",EDGE,"E2.left"),sQuery(id+"F5.wireOp",EDGE,"E2.right")])],"isStart":true})]}),makeQuery(id+"F10.opExtrude","SWEPT_FACE",FACE,{"disambiguationData":[OSD([sQuery(id+"F9.wireOp",EDGE,"E4.bottom")])]}),makeQuery(id+"F10.opExtrude","SWEPT_FACE",FACE,{"disambiguationData":[OSD([sQuery(id+"F9.wireOp",EDGE,"E7.bottom")])]})]}),makeQuery(id+"F12.opExtrude","SWEPT_FACE",FACE,{"disambiguationData":[OSD([sQuery(id+"F11.wireOp",EDGE,"E9.bottom")])]})]}),makeQuery(id+"F18.opExtrude","CAP_FACE",FACE,{"disambiguationData":[OSD([sQuery(id+"F17.wireOp",EDGE,"E16.bottom"),sQuery(id+"F17.wireOp",EDGE,"E16.top"),sQuery(id+"F17.wireOp",EDGE,"E16.left"),sQuery(id+"F17.wireOp",EDGE,"E16.right")])],"isStart":true})]}),makeQuery(id+"F20.opExtrude","CAP_FACE",FACE,{"disambiguationData":[OSD([sQuery(id+"F19.wireOp",EDGE,"E17.bottom"),sQuery(id+"F19.wireOp",EDGE,"E17.top"),sQuery(id+"F19.wireOp",EDGE,"E17.left"),sQuery(id+"F19.wireOp",EDGE,"E17.right")])],"isStart":true})]}),makeQuery(id+"F22.opExtrude","CAP_FACE",FACE,{"disambiguationData":[OSD([sQuery(id+"F21.wireOp",EDGE,"E18.bottom"),sQuery(id+"F21.wireOp",EDGE,"E18.top"),sQuery(id+"F21.wireOp",EDGE,"E18.left"),sQuery(id+"F21.wireOp",EDGE,"E18.right")])],"isStart":false})]}),makeQuery(id+"F24.opExtrude","CAP_FACE",FACE,{"disambiguationData":[OSD([sQuery(id+"F23.wireOp",EDGE,"E19.bottom"),sQuery(id+"F23.wireOp",EDGE,"E19.top"),sQuery(id+"F23.wireOp",EDGE,"E19.left"),sQuery(id+"F23.wireOp",EDGE,"E19.right")])],"isStart":true}),makeQuery(id+"F24.opExtrude","CAP_FACE",FACE,{"disambiguationData":[OSD([sQuery(id+"F23.wireOp",EDGE,"E20.bottom"),sQuery(id+"F23.wireOp",EDGE,"E20.top"),sQuery(id+"F23.wireOp",EDGE,"E20.left"),sQuery(id+"F23.wireOp",EDGE,"E20.right")])],"isStart":true})]}),makeQuery(id+"F26.opExtrude","CAP_FACE",FACE,{"disambiguationData":[OSD([sQuery(id+"F25.wireOp",EDGE,"E21.bottom"),sQuery(id+"F25.wireOp",EDGE,"E21.top"),sQuery(id+"F25.wireOp",EDGE,"E21.left"),sQuery(id+"F25.wireOp",EDGE,"E21.right")])],"isStart":true})]}),makeQuery(id+"F28.opExtrude","CAP_FACE",FACE,{"disambiguationData":[OSD([sQuery(id+"F27.wireOp",EDGE,"E22.bottom"),sQuery(id+"F27.wireOp",EDGE,"E22.top"),sQuery(id+"F27.wireOp",EDGE,"E22.left"),sQuery(id+"F27.wireOp",EDGE,"E22.right")])],"isStart":true})]});
            var sketch = newSketch(context, id + "F29", { "sketchPlane" : qUnion([Q0])});
            skLineSegment(sketch, "E23.bottom", {"start": v(736.6, 254) * mm, "end": v(755.62, 254) * mm});
            skLineSegment(sketch, "E23.top", {"start": v(736.6, 393.7) * mm, "end": v(755.62, 393.7) * mm});
            skLineSegment(sketch, "E23.left", {"start": v(736.6, 254) * mm, "end": v(736.6, 393.7) * mm});
            skLineSegment(sketch, "E23.right", {"start": v(755.62, 254) * mm, "end": v(755.62, 393.7) * mm});
            skSolve(sketch);
        }
        {
            var Q0;
            Q0=makeQuery(id+"F29.imprint","IMPRINT",FACE,{"disambiguationData":[TD([[makeQuery(id+"F29.imprint","IMPRINT",EDGE,{"derivedFrom":sQuery(id+"F29.wireOp",EDGE,"E23.bottom")}),1.0]])]});
            extrude(context, id + "F30", {"entities" : qUnion([Q0]), "operationType" : NewBodyOperationType.ADD, "oppositeDirection" : true, "depth" : 406.4 * mm, "offsetDistance" : 25.4 * mm});
        }
        {
            var Q0;
            Q0=makeQuery(id+"F30.boolean.opBoolean","MERGE",FACE,{"derivedFrom":[makeQuery(id+"F28.boolean.opBoolean","MERGE",FACE,{"derivedFrom":[makeQuery(id+"F26.boolean.opBoolean","MERGE",FACE,{"derivedFrom":[makeQuery(id+"F24.boolean.opBoolean","MERGE",FACE,{"derivedFrom":[makeQuery(id+"F22.boolean.opBoolean","MERGE",FACE,{"derivedFrom":[makeQuery(id+"F20.boolean.opBoolean","MERGE",FACE,{"derivedFrom":[makeQuery(id+"F18.boolean.opBoolean","MERGE",FACE,{"derivedFrom":[makeQuery(id+"F12.boolean.opBoolean","MERGE",FACE,{"derivedFrom":[makeQuery(id+"F10.boolean.opBoolean","MERGE",FACE,{"derivedFrom":[makeQuery(id+"F6.boolean.opBoolean","MERGE",FACE,{"derivedFrom":[makeQuery(id+"F4.boolean.opBoolean","MERGE",FACE,{"derivedFrom":[makeQuery(id+"F1.opExtrude","CAP_FACE",FACE,{"disambiguationData":[OSD([sQuery(id+"F0.wireOp",EDGE,"E0.bottom"),sQuery(id+"F0.wireOp",EDGE,"E0.top"),sQuery(id+"F0.wireOp",EDGE,"E0.left"),sQuery(id+"F0.wireOp",EDGE,"E0.right")])],"isStart":false}),makeQuery(id+"F4.opExtrude","SWEPT_FACE",FACE,{"disambiguationData":[OSD([sQuery(id+"F2.wireOp",EDGE,"E1.bottom")])]})]}),makeQuery(id+"F6.opExtrude","CAP_FACE",FACE,{"disambiguationData":[OSD([sQuery(id+"F5.wireOp",EDGE,"E2.bottom"),sQuery(id+"F5.wireOp",EDGE,"E2.top"),sQuery(id+"F5.wireOp",EDGE,"E2.left"),sQuery(id+"F5.wireOp",EDGE,"E2.right")])],"isStart":true})]}),makeQuery(id+"F10.opExtrude","SWEPT_FACE",FACE,{"disambiguationData":[OSD([sQuery(id+"F9.wireOp",EDGE,"E4.bottom")])]}),makeQuery(id+"F10.opExtrude","SWEPT_FACE",FACE,{"disambiguationData":[OSD([sQuery(id+"F9.wireOp",EDGE,"E7.bottom")])]})]}),makeQuery(id+"F12.opExtrude","SWEPT_FACE",FACE,{"disambiguationData":[OSD([sQuery(id+"F11.wireOp",EDGE,"E9.bottom")])]})]}),makeQuery(id+"F18.opExtrude","CAP_FACE",FACE,{"disambiguationData":[OSD([sQuery(id+"F17.wireOp",EDGE,"E16.bottom"),sQuery(id+"F17.wireOp",EDGE,"E16.top"),sQuery(id+"F17.wireOp",EDGE,"E16.left"),sQuery(id+"F17.wireOp",EDGE,"E16.right")])],"isStart":true})]}),makeQuery(id+"F20.opExtrude","CAP_FACE",FACE,{"disambiguationData":[OSD([sQuery(id+"F19.wireOp",EDGE,"E17.bottom"),sQuery(id+"F19.wireOp",EDGE,"E17.top"),sQuery(id+"F19.wireOp",EDGE,"E17.left"),sQuery(id+"F19.wireOp",EDGE,"E17.right")])],"isStart":true})]}),makeQuery(id+"F22.opExtrude","CAP_FACE",FACE,{"disambiguationData":[OSD([sQuery(id+"F21.wireOp",EDGE,"E18.bottom"),sQuery(id+"F21.wireOp",EDGE,"E18.top"),sQuery(id+"F21.wireOp",EDGE,"E18.left"),sQuery(id+"F21.wireOp",EDGE,"E18.right")])],"isStart":false})]}),makeQuery(id+"F24.opExtrude","CAP_FACE",FACE,{"disambiguationData":[OSD([sQuery(id+"F23.wireOp",EDGE,"E19.bottom"),sQuery(id+"F23.wireOp",EDGE,"E19.top"),sQuery(id+"F23.wireOp",EDGE,"E19.left"),sQuery(id+"F23.wireOp",EDGE,"E19.right")])],"isStart":true}),makeQuery(id+"F24.opExtrude","CAP_FACE",FACE,{"disambiguationData":[OSD([sQuery(id+"F23.wireOp",EDGE,"E20.bottom"),sQuery(id+"F23.wireOp",EDGE,"E20.top"),sQuery(id+"F23.wireOp",EDGE,"E20.left"),sQuery(id+"F23.wireOp",EDGE,"E20.right")])],"isStart":true})]}),makeQuery(id+"F26.opExtrude","CAP_FACE",FACE,{"disambiguationData":[OSD([sQuery(id+"F25.wireOp",EDGE,"E21.bottom"),sQuery(id+"F25.wireOp",EDGE,"E21.top"),sQuery(id+"F25.wireOp",EDGE,"E21.left"),sQuery(id+"F25.wireOp",EDGE,"E21.right")])],"isStart":true})]}),makeQuery(id+"F28.opExtrude","CAP_FACE",FACE,{"disambiguationData":[OSD([sQuery(id+"F27.wireOp",EDGE,"E22.bottom"),sQuery(id+"F27.wireOp",EDGE,"E22.top"),sQuery(id+"F27.wireOp",EDGE,"E22.left"),sQuery(id+"F27.wireOp",EDGE,"E22.right")])],"isStart":true})]}),makeQuery(id+"F30.opExtrude","CAP_FACE",FACE,{"disambiguationData":[OSD([sQuery(id+"F29.wireOp",EDGE,"E23.bottom"),sQuery(id+"F29.wireOp",EDGE,"E23.top"),sQuery(id+"F29.wireOp",EDGE,"E23.left"),sQuery(id+"F29.wireOp",EDGE,"E23.right")])],"isStart":true})]});
            var sketch = newSketch(context, id + "F31", { "sketchPlane" : qUnion([Q0])});
            skLineSegment(sketch, "E24.bottom", {"start": v(0, 114.3) * mm, "end": v(-19.05, 114.3) * mm});
            skLineSegment(sketch, "E24.top", {"start": v(0, 254) * mm, "end": v(-19.05, 254) * mm});
            skLineSegment(sketch, "E24.left", {"start": v(0, 114.3) * mm, "end": v(0, 254) * mm});
            skLineSegment(sketch, "E24.right", {"start": v(-19.05, 114.3) * mm, "end": v(-19.05, 254) * mm});
            skLineSegment(sketch, "E25.bottom", {"start": v(0, 114.3) * mm, "end": v(-19.02, 114.3) * mm});
            skLineSegment(sketch, "E25.top", {"start": v(0, -25.4) * mm, "end": v(-19.02, -25.4) * mm});
            skLineSegment(sketch, "E25.left", {"start": v(0, 114.3) * mm, "end": v(0, -25.4) * mm});
            skLineSegment(sketch, "E25.right", {"start": v(-19.02, 114.3) * mm, "end": v(-19.02, -25.4) * mm});
            skLineSegment(sketch, "E26.bottom", {"start": v(0, 254) * mm, "end": v(-19.02, 254) * mm});
            skLineSegment(sketch, "E26.top", {"start": v(0, 393.7) * mm, "end": v(-19.02, 393.7) * mm});
            skLineSegment(sketch, "E26.left", {"start": v(0, 254) * mm, "end": v(0, 393.7) * mm});
            skLineSegment(sketch, "E26.right", {"start": v(-19.02, 254) * mm, "end": v(-19.02, 393.7) * mm});
            skSolve(sketch);
        }
        {
            var Q0;
            Q0=makeQuery(id+"F31.imprint","IMPRINT",FACE,{"disambiguationData":[TD([[makeQuery(id+"F31.imprint","IMPRINT",EDGE,{"derivedFrom":sQuery(id+"F31.wireOp",EDGE,"E26.bottom")}),-1.0]])]});
            var Q1;
            Q1=makeQuery(id+"F31.imprint","IMPRINT",FACE,{"disambiguationData":[TD([[makeQuery(id+"F31.imprint","IMPRINT",EDGE,{"derivedFrom":sQuery(id+"F31.wireOp",EDGE,"E24.bottom")}),-1.0]])]});
            var Q2;
            Q2=makeQuery(id+"F31.imprint","IMPRINT",FACE,{"disambiguationData":[TD([[makeQuery(id+"F31.imprint","IMPRINT",EDGE,{"derivedFrom":sQuery(id+"F31.wireOp",EDGE,"E25.bottom")}),1.0]])]});
            extrude(context, id + "F32", {"entities" : qUnion([Q0, Q1, Q2]), "operationType" : NewBodyOperationType.ADD, "oppositeDirection" : true, "depth" : 406.4 * mm, "offsetDistance" : 25.4 * mm});
        }
        {
            var Q0;
            Q0=makeQuery(id+"F32.boolean.opBoolean","MERGE",FACE,{"derivedFrom":[makeQuery(id+"F30.boolean.opBoolean","MERGE",FACE,{"derivedFrom":[makeQuery(id+"F28.boolean.opBoolean","MERGE",FACE,{"derivedFrom":[makeQuery(id+"F26.boolean.opBoolean","MERGE",FACE,{"derivedFrom":[makeQuery(id+"F24.boolean.opBoolean","MERGE",FACE,{"derivedFrom":[makeQuery(id+"F22.boolean.opBoolean","MERGE",FACE,{"derivedFrom":[makeQuery(id+"F20.boolean.opBoolean","MERGE",FACE,{"derivedFrom":[makeQuery(id+"F18.boolean.opBoolean","MERGE",FACE,{"derivedFrom":[makeQuery(id+"F12.boolean.opBoolean","MERGE",FACE,{"derivedFrom":[makeQuery(id+"F10.boolean.opBoolean","MERGE",FACE,{"derivedFrom":[makeQuery(id+"F6.boolean.opBoolean","MERGE",FACE,{"derivedFrom":[makeQuery(id+"F4.boolean.opBoolean","MERGE",FACE,{"derivedFrom":[makeQuery(id+"F1.opExtrude","CAP_FACE",FACE,{"disambiguationData":[OSD([sQuery(id+"F0.wireOp",EDGE,"E0.bottom"),sQuery(id+"F0.wireOp",EDGE,"E0.top"),sQuery(id+"F0.wireOp",EDGE,"E0.left"),sQuery(id+"F0.wireOp",EDGE,"E0.right")])],"isStart":false}),makeQuery(id+"F4.opExtrude","SWEPT_FACE",FACE,{"disambiguationData":[OSD([sQuery(id+"F2.wireOp",EDGE,"E1.bottom")])]})]}),makeQuery(id+"F6.opExtrude","CAP_FACE",FACE,{"disambiguationData":[OSD([sQuery(id+"F5.wireOp",EDGE,"E2.bottom"),sQuery(id+"F5.wireOp",EDGE,"E2.top"),sQuery(id+"F5.wireOp",EDGE,"E2.left"),sQuery(id+"F5.wireOp",EDGE,"E2.right")])],"isStart":true})]}),makeQuery(id+"F10.opExtrude","SWEPT_FACE",FACE,{"disambiguationData":[OSD([sQuery(id+"F9.wireOp",EDGE,"E4.bottom")])]}),makeQuery(id+"F10.opExtrude","SWEPT_FACE",FACE,{"disambiguationData":[OSD([sQuery(id+"F9.wireOp",EDGE,"E7.bottom")])]})]}),makeQuery(id+"F12.opExtrude","SWEPT_FACE",FACE,{"disambiguationData":[OSD([sQuery(id+"F11.wireOp",EDGE,"E9.bottom")])]})]}),makeQuery(id+"F18.opExtrude","CAP_FACE",FACE,{"disambiguationData":[OSD([sQuery(id+"F17.wireOp",EDGE,"E16.bottom"),sQuery(id+"F17.wireOp",EDGE,"E16.top"),sQuery(id+"F17.wireOp",EDGE,"E16.left"),sQuery(id+"F17.wireOp",EDGE,"E16.right")])],"isStart":true})]}),makeQuery(id+"F20.opExtrude","CAP_FACE",FACE,{"disambiguationData":[OSD([sQuery(id+"F19.wireOp",EDGE,"E17.bottom"),sQuery(id+"F19.wireOp",EDGE,"E17.top"),sQuery(id+"F19.wireOp",EDGE,"E17.left"),sQuery(id+"F19.wireOp",EDGE,"E17.right")])],"isStart":true})]}),makeQuery(id+"F22.opExtrude","CAP_FACE",FACE,{"disambiguationData":[OSD([sQuery(id+"F21.wireOp",EDGE,"E18.bottom"),sQuery(id+"F21.wireOp",EDGE,"E18.top"),sQuery(id+"F21.wireOp",EDGE,"E18.left"),sQuery(id+"F21.wireOp",EDGE,"E18.right")])],"isStart":false})]}),makeQuery(id+"F24.opExtrude","CAP_FACE",FACE,{"disambiguationData":[OSD([sQuery(id+"F23.wireOp",EDGE,"E19.bottom"),sQuery(id+"F23.wireOp",EDGE,"E19.top"),sQuery(id+"F23.wireOp",EDGE,"E19.left"),sQuery(id+"F23.wireOp",EDGE,"E19.right")])],"isStart":true}),makeQuery(id+"F24.opExtrude","CAP_FACE",FACE,{"disambiguationData":[OSD([sQuery(id+"F23.wireOp",EDGE,"E20.bottom"),sQuery(id+"F23.wireOp",EDGE,"E20.top"),sQuery(id+"F23.wireOp",EDGE,"E20.left"),sQuery(id+"F23.wireOp",EDGE,"E20.right")])],"isStart":true})]}),makeQuery(id+"F26.opExtrude","CAP_FACE",FACE,{"disambiguationData":[OSD([sQuery(id+"F25.wireOp",EDGE,"E21.bottom"),sQuery(id+"F25.wireOp",EDGE,"E21.top"),sQuery(id+"F25.wireOp",EDGE,"E21.left"),sQuery(id+"F25.wireOp",EDGE,"E21.right")])],"isStart":true})]}),makeQuery(id+"F28.opExtrude","CAP_FACE",FACE,{"disambiguationData":[OSD([sQuery(id+"F27.wireOp",EDGE,"E22.bottom"),sQuery(id+"F27.wireOp",EDGE,"E22.top"),sQuery(id+"F27.wireOp",EDGE,"E22.left"),sQuery(id+"F27.wireOp",EDGE,"E22.right")])],"isStart":true})]}),makeQuery(id+"F30.opExtrude","CAP_FACE",FACE,{"disambiguationData":[OSD([sQuery(id+"F29.wireOp",EDGE,"E23.bottom"),sQuery(id+"F29.wireOp",EDGE,"E23.top"),sQuery(id+"F29.wireOp",EDGE,"E23.left"),sQuery(id+"F29.wireOp",EDGE,"E23.right")])],"isStart":true})]}),makeQuery(id+"F32.opExtrude","CAP_FACE",FACE,{"disambiguationData":[OSD([sQuery(id+"F31.wireOp",EDGE,"E24.bottom"),sQuery(id+"F31.wireOp",EDGE,"E24.top"),sQuery(id+"F31.wireOp",EDGE,"E24.left"),sQuery(id+"F31.wireOp",EDGE,"E24.right"),sQuery(id+"F31.wireOp",EDGE,"E25.top"),sQuery(id+"F31.wireOp",EDGE,"E25.left"),sQuery(id+"F31.wireOp",EDGE,"E25.right"),sQuery(id+"F31.wireOp",EDGE,"E26.top"),sQuery(id+"F31.wireOp",EDGE,"E26.left"),sQuery(id+"F31.wireOp",EDGE,"E26.right")])],"isStart":true})]});
            var sketch = newSketch(context, id + "F33", { "sketchPlane" : qUnion([Q0])});
            skLineSegment(sketch, "E27.bottom", {"start": v(298.45, 406.4) * mm, "end": v(438.15, 406.4) * mm});
            skLineSegment(sketch, "E27.top", {"start": v(298.45, 425.45) * mm, "end": v(438.15, 425.45) * mm});
            skLineSegment(sketch, "E27.left", {"start": v(298.45, 406.4) * mm, "end": v(298.45, 425.45) * mm});
            skLineSegment(sketch, "E27.right", {"start": v(438.15, 406.4) * mm, "end": v(438.15, 425.45) * mm});
            skLineSegment(sketch, "E28.bottom", {"start": v(438.15, 406.4) * mm, "end": v(577.85, 406.4) * mm});
            skLineSegment(sketch, "E28.top", {"start": v(438.15, 425.42) * mm, "end": v(577.85, 425.42) * mm});
            skLineSegment(sketch, "E28.left", {"start": v(438.15, 406.4) * mm, "end": v(438.15, 425.42) * mm});
            skLineSegment(sketch, "E28.right", {"start": v(577.85, 406.4) * mm, "end": v(577.85, 425.42) * mm});
            skLineSegment(sketch, "E29.bottom", {"start": v(577.85, 406.4) * mm, "end": v(717.55, 406.4) * mm});
            skLineSegment(sketch, "E29.top", {"start": v(577.85, 425.45) * mm, "end": v(717.55, 425.45) * mm});
            skLineSegment(sketch, "E29.left", {"start": v(577.85, 406.4) * mm, "end": v(577.85, 425.45) * mm});
            skLineSegment(sketch, "E29.right", {"start": v(717.55, 406.4) * mm, "end": v(717.55, 425.45) * mm});
            skLineSegment(sketch, "E30.bottom", {"start": v(298.45, 406.4) * mm, "end": v(158.75, 406.4) * mm});
            skLineSegment(sketch, "E30.top", {"start": v(298.45, 425.42) * mm, "end": v(158.75, 425.42) * mm});
            skLineSegment(sketch, "E30.left", {"start": v(298.45, 406.4) * mm, "end": v(298.45, 425.42) * mm});
            skLineSegment(sketch, "E30.right", {"start": v(158.75, 406.4) * mm, "end": v(158.75, 425.42) * mm});
            skLineSegment(sketch, "E31.bottom", {"start": v(158.75, 406.4) * mm, "end": v(19.05, 406.4) * mm});
            skLineSegment(sketch, "E31.top", {"start": v(158.75, 425.45) * mm, "end": v(19.05, 425.45) * mm});
            skLineSegment(sketch, "E31.left", {"start": v(158.75, 406.4) * mm, "end": v(158.75, 425.45) * mm});
            skLineSegment(sketch, "E31.right", {"start": v(19.05, 406.4) * mm, "end": v(19.05, 425.45) * mm});
            skSolve(sketch);
        }
        {
            var Q0;
            {var subQ3=sQuery(id+"F33.wireOp",EDGE,"E31.bottom");Q0=makeQuery(id+"F33.imprint","IMPRINT",FACE,{"disambiguationData":[TD([[makeQuery(id+"F33.imprint","IMPRINT",EDGE,{"derivedFrom":subQ3}),1.0]])]});}
            var Q1;
            {var subQ0=sQuery(id+"F33.wireOp",EDGE,"E30.bottom");Q1=makeQuery(id+"F33.imprint","IMPRINT",FACE,{"disambiguationData":[TD([[makeQuery(id+"F33.imprint","IMPRINT",EDGE,{"derivedFrom":subQ0}),1.0]])]});}
            var Q2;
            Q2=makeQuery(id+"F33.imprint","IMPRINT",FACE,{"disambiguationData":[TD([[makeQuery(id+"F33.imprint","IMPRINT",EDGE,{"derivedFrom":sQuery(id+"F33.wireOp",EDGE,"E27.bottom")}),1.0]])]});
            var Q3;
            {var subQ0=sQuery(id+"F33.wireOp",EDGE,"E28.bottom");Q3=makeQuery(id+"F33.imprint","IMPRINT",FACE,{"disambiguationData":[TD([[makeQuery(id+"F33.imprint","IMPRINT",EDGE,{"derivedFrom":subQ0}),1.0]])]});}
            var Q4;
            {var subQ3=sQuery(id+"F33.wireOp",EDGE,"E29.bottom");Q4=makeQuery(id+"F33.imprint","IMPRINT",FACE,{"disambiguationData":[TD([[makeQuery(id+"F33.imprint","IMPRINT",EDGE,{"derivedFrom":subQ3}),1.0]])]});}
            extrude(context, id + "F34", {"entities" : qUnion([Q0, Q1, Q2, Q3, Q4]), "operationType" : NewBodyOperationType.ADD, "oppositeDirection" : true, "depth" : 406.4 * mm, "offsetDistance" : 25.4 * mm});
        }
        {
            var Q0;
            Q0=makeQuery(id+"F34.boolean.opBoolean","MERGE",FACE,{"derivedFrom":[makeQuery(id+"F32.boolean.opBoolean","MERGE",FACE,{"derivedFrom":[makeQuery(id+"F30.boolean.opBoolean","MERGE",FACE,{"derivedFrom":[makeQuery(id+"F28.boolean.opBoolean","MERGE",FACE,{"derivedFrom":[makeQuery(id+"F26.boolean.opBoolean","MERGE",FACE,{"derivedFrom":[makeQuery(id+"F24.boolean.opBoolean","MERGE",FACE,{"derivedFrom":[makeQuery(id+"F22.boolean.opBoolean","MERGE",FACE,{"derivedFrom":[makeQuery(id+"F20.boolean.opBoolean","MERGE",FACE,{"derivedFrom":[makeQuery(id+"F18.boolean.opBoolean","MERGE",FACE,{"derivedFrom":[makeQuery(id+"F12.boolean.opBoolean","MERGE",FACE,{"derivedFrom":[makeQuery(id+"F10.boolean.opBoolean","MERGE",FACE,{"derivedFrom":[makeQuery(id+"F6.boolean.opBoolean","MERGE",FACE,{"derivedFrom":[makeQuery(id+"F4.boolean.opBoolean","MERGE",FACE,{"derivedFrom":[makeQuery(id+"F1.opExtrude","CAP_FACE",FACE,{"disambiguationData":[OSD([sQuery(id+"F0.wireOp",EDGE,"E0.bottom"),sQuery(id+"F0.wireOp",EDGE,"E0.top"),sQuery(id+"F0.wireOp",EDGE,"E0.left"),sQuery(id+"F0.wireOp",EDGE,"E0.right")])],"isStart":false}),makeQuery(id+"F4.opExtrude","SWEPT_FACE",FACE,{"disambiguationData":[OSD([sQuery(id+"F2.wireOp",EDGE,"E1.bottom")])]})]}),makeQuery(id+"F6.opExtrude","CAP_FACE",FACE,{"disambiguationData":[OSD([sQuery(id+"F5.wireOp",EDGE,"E2.bottom"),sQuery(id+"F5.wireOp",EDGE,"E2.top"),sQuery(id+"F5.wireOp",EDGE,"E2.left"),sQuery(id+"F5.wireOp",EDGE,"E2.right")])],"isStart":true})]}),makeQuery(id+"F10.opExtrude","SWEPT_FACE",FACE,{"disambiguationData":[OSD([sQuery(id+"F9.wireOp",EDGE,"E4.bottom")])]}),makeQuery(id+"F10.opExtrude","SWEPT_FACE",FACE,{"disambiguationData":[OSD([sQuery(id+"F9.wireOp",EDGE,"E7.bottom")])]})]}),makeQuery(id+"F12.opExtrude","SWEPT_FACE",FACE,{"disambiguationData":[OSD([sQuery(id+"F11.wireOp",EDGE,"E9.bottom")])]})]}),makeQuery(id+"F18.opExtrude","CAP_FACE",FACE,{"disambiguationData":[OSD([sQuery(id+"F17.wireOp",EDGE,"E16.bottom"),sQuery(id+"F17.wireOp",EDGE,"E16.top"),sQuery(id+"F17.wireOp",EDGE,"E16.left"),sQuery(id+"F17.wireOp",EDGE,"E16.right")])],"isStart":true})]}),makeQuery(id+"F20.opExtrude","CAP_FACE",FACE,{"disambiguationData":[OSD([sQuery(id+"F19.wireOp",EDGE,"E17.bottom"),sQuery(id+"F19.wireOp",EDGE,"E17.top"),sQuery(id+"F19.wireOp",EDGE,"E17.left"),sQuery(id+"F19.wireOp",EDGE,"E17.right")])],"isStart":true})]}),makeQuery(id+"F22.opExtrude","CAP_FACE",FACE,{"disambiguationData":[OSD([sQuery(id+"F21.wireOp",EDGE,"E18.bottom"),sQuery(id+"F21.wireOp",EDGE,"E18.top"),sQuery(id+"F21.wireOp",EDGE,"E18.left"),sQuery(id+"F21.wireOp",EDGE,"E18.right")])],"isStart":false})]}),makeQuery(id+"F24.opExtrude","CAP_FACE",FACE,{"disambiguationData":[OSD([sQuery(id+"F23.wireOp",EDGE,"E19.bottom"),sQuery(id+"F23.wireOp",EDGE,"E19.top"),sQuery(id+"F23.wireOp",EDGE,"E19.left"),sQuery(id+"F23.wireOp",EDGE,"E19.right")])],"isStart":true}),makeQuery(id+"F24.opExtrude","CAP_FACE",FACE,{"disambiguationData":[OSD([sQuery(id+"F23.wireOp",EDGE,"E20.bottom"),sQuery(id+"F23.wireOp",EDGE,"E20.top"),sQuery(id+"F23.wireOp",EDGE,"E20.left"),sQuery(id+"F23.wireOp",EDGE,"E20.right")])],"isStart":true})]}),makeQuery(id+"F26.opExtrude","CAP_FACE",FACE,{"disambiguationData":[OSD([sQuery(id+"F25.wireOp",EDGE,"E21.bottom"),sQuery(id+"F25.wireOp",EDGE,"E21.top"),sQuery(id+"F25.wireOp",EDGE,"E21.left"),sQuery(id+"F25.wireOp",EDGE,"E21.right")])],"isStart":true})]}),makeQuery(id+"F28.opExtrude","CAP_FACE",FACE,{"disambiguationData":[OSD([sQuery(id+"F27.wireOp",EDGE,"E22.bottom"),sQuery(id+"F27.wireOp",EDGE,"E22.top"),sQuery(id+"F27.wireOp",EDGE,"E22.left"),sQuery(id+"F27.wireOp",EDGE,"E22.right")])],"isStart":true})]}),makeQuery(id+"F30.opExtrude","CAP_FACE",FACE,{"disambiguationData":[OSD([sQuery(id+"F29.wireOp",EDGE,"E23.bottom"),sQuery(id+"F29.wireOp",EDGE,"E23.top"),sQuery(id+"F29.wireOp",EDGE,"E23.left"),sQuery(id+"F29.wireOp",EDGE,"E23.right")])],"isStart":true})]}),makeQuery(id+"F32.opExtrude","CAP_FACE",FACE,{"disambiguationData":[OSD([sQuery(id+"F31.wireOp",EDGE,"E24.bottom"),sQuery(id+"F31.wireOp",EDGE,"E24.top"),sQuery(id+"F31.wireOp",EDGE,"E24.left"),sQuery(id+"F31.wireOp",EDGE,"E24.right"),sQuery(id+"F31.wireOp",EDGE,"E25.top"),sQuery(id+"F31.wireOp",EDGE,"E25.left"),sQuery(id+"F31.wireOp",EDGE,"E25.right"),sQuery(id+"F31.wireOp",EDGE,"E26.top"),sQuery(id+"F31.wireOp",EDGE,"E26.left"),sQuery(id+"F31.wireOp",EDGE,"E26.right")])],"isStart":true})]}),makeQuery(id+"F34.opExtrude","CAP_FACE",FACE,{"disambiguationData":[OSD([sQuery(id+"F33.wireOp",EDGE,"E27.bottom"),sQuery(id+"F33.wireOp",EDGE,"E27.top"),sQuery(id+"F33.wireOp",EDGE,"E27.left"),sQuery(id+"F33.wireOp",EDGE,"E27.right"),sQuery(id+"F33.wireOp",EDGE,"E28.bottom"),sQuery(id+"F33.wireOp",EDGE,"E28.top"),sQuery(id+"F33.wireOp",EDGE,"E29.bottom"),sQuery(id+"F33.wireOp",EDGE,"E29.top"),sQuery(id+"F33.wireOp",EDGE,"E29.left"),sQuery(id+"F33.wireOp",EDGE,"E29.right"),sQuery(id+"F33.wireOp",EDGE,"E30.bottom"),sQuery(id+"F33.wireOp",EDGE,"E30.top"),sQuery(id+"F33.wireOp",EDGE,"E31.bottom"),sQuery(id+"F33.wireOp",EDGE,"E31.top"),sQuery(id+"F33.wireOp",EDGE,"E31.left"),sQuery(id+"F33.wireOp",EDGE,"E31.right")])],"isStart":true})]});
            var sketch = newSketch(context, id + "F35", { "sketchPlane" : qUnion([Q0])});
            skLineSegment(sketch, "E32.bottom", {"start": v(755.62, 31.75) * mm, "end": v(774.67, 31.75) * mm});
            skLineSegment(sketch, "E32.top", {"start": v(755.62, -57.15) * mm, "end": v(774.67, -57.15) * mm});
            skLineSegment(sketch, "E32.left", {"start": v(755.62, 31.75) * mm, "end": v(755.62, -57.15) * mm});
            skLineSegment(sketch, "E32.right", {"start": v(774.67, 31.75) * mm, "end": v(774.67, -57.15) * mm});
            skSolve(sketch);
        }
        {
            var Q0;
            {var subQ3=sQuery(id+"F35.wireOp",EDGE,"E32.bottom");Q0=makeQuery(id+"F35.imprint","IMPRINT",FACE,{"disambiguationData":[TD([[makeQuery(id+"F35.imprint","IMPRINT",EDGE,{"derivedFrom":subQ3}),-1.0]])]});}
            extrude(context, id + "F36", {"entities" : qUnion([Q0]), "operationType" : NewBodyOperationType.ADD, "oppositeDirection" : true, "depth" : 406.4 * mm, "offsetDistance" : 25.4 * mm});
        }
        {
            var Q0;
            Q0=makeQuery(id+"F36.boolean.opBoolean","MERGE",FACE,{"derivedFrom":[makeQuery(id+"F34.boolean.opBoolean","MERGE",FACE,{"derivedFrom":[makeQuery(id+"F32.boolean.opBoolean","MERGE",FACE,{"derivedFrom":[makeQuery(id+"F30.boolean.opBoolean","MERGE",FACE,{"derivedFrom":[makeQuery(id+"F28.boolean.opBoolean","MERGE",FACE,{"derivedFrom":[makeQuery(id+"F26.boolean.opBoolean","MERGE",FACE,{"derivedFrom":[makeQuery(id+"F24.boolean.opBoolean","MERGE",FACE,{"derivedFrom":[makeQuery(id+"F22.boolean.opBoolean","MERGE",FACE,{"derivedFrom":[makeQuery(id+"F20.boolean.opBoolean","MERGE",FACE,{"derivedFrom":[makeQuery(id+"F18.boolean.opBoolean","MERGE",FACE,{"derivedFrom":[makeQuery(id+"F12.boolean.opBoolean","MERGE",FACE,{"derivedFrom":[makeQuery(id+"F10.boolean.opBoolean","MERGE",FACE,{"derivedFrom":[makeQuery(id+"F6.boolean.opBoolean","MERGE",FACE,{"derivedFrom":[makeQuery(id+"F4.boolean.opBoolean","MERGE",FACE,{"derivedFrom":[makeQuery(id+"F1.opExtrude","CAP_FACE",FACE,{"disambiguationData":[OSD([sQuery(id+"F0.wireOp",EDGE,"E0.bottom"),sQuery(id+"F0.wireOp",EDGE,"E0.top"),sQuery(id+"F0.wireOp",EDGE,"E0.left"),sQuery(id+"F0.wireOp",EDGE,"E0.right")])],"isStart":false}),makeQuery(id+"F4.opExtrude","SWEPT_FACE",FACE,{"disambiguationData":[OSD([sQuery(id+"F2.wireOp",EDGE,"E1.bottom")])]})]}),makeQuery(id+"F6.opExtrude","CAP_FACE",FACE,{"disambiguationData":[OSD([sQuery(id+"F5.wireOp",EDGE,"E2.bottom"),sQuery(id+"F5.wireOp",EDGE,"E2.top"),sQuery(id+"F5.wireOp",EDGE,"E2.left"),sQuery(id+"F5.wireOp",EDGE,"E2.right")])],"isStart":true})]}),makeQuery(id+"F10.opExtrude","SWEPT_FACE",FACE,{"disambiguationData":[OSD([sQuery(id+"F9.wireOp",EDGE,"E4.bottom")])]}),makeQuery(id+"F10.opExtrude","SWEPT_FACE",FACE,{"disambiguationData":[OSD([sQuery(id+"F9.wireOp",EDGE,"E7.bottom")])]})]}),makeQuery(id+"F12.opExtrude","SWEPT_FACE",FACE,{"disambiguationData":[OSD([sQuery(id+"F11.wireOp",EDGE,"E9.bottom")])]})]}),makeQuery(id+"F18.opExtrude","CAP_FACE",FACE,{"disambiguationData":[OSD([sQuery(id+"F17.wireOp",EDGE,"E16.bottom"),sQuery(id+"F17.wireOp",EDGE,"E16.top"),sQuery(id+"F17.wireOp",EDGE,"E16.left"),sQuery(id+"F17.wireOp",EDGE,"E16.right")])],"isStart":true})]}),makeQuery(id+"F20.opExtrude","CAP_FACE",FACE,{"disambiguationData":[OSD([sQuery(id+"F19.wireOp",EDGE,"E17.bottom"),sQuery(id+"F19.wireOp",EDGE,"E17.top"),sQuery(id+"F19.wireOp",EDGE,"E17.left"),sQuery(id+"F19.wireOp",EDGE,"E17.right")])],"isStart":true})]}),makeQuery(id+"F22.opExtrude","CAP_FACE",FACE,{"disambiguationData":[OSD([sQuery(id+"F21.wireOp",EDGE,"E18.bottom"),sQuery(id+"F21.wireOp",EDGE,"E18.top"),sQuery(id+"F21.wireOp",EDGE,"E18.left"),sQuery(id+"F21.wireOp",EDGE,"E18.right")])],"isStart":false})]}),makeQuery(id+"F24.opExtrude","CAP_FACE",FACE,{"disambiguationData":[OSD([sQuery(id+"F23.wireOp",EDGE,"E19.bottom"),sQuery(id+"F23.wireOp",EDGE,"E19.top"),sQuery(id+"F23.wireOp",EDGE,"E19.left"),sQuery(id+"F23.wireOp",EDGE,"E19.right")])],"isStart":true}),makeQuery(id+"F24.opExtrude","CAP_FACE",FACE,{"disambiguationData":[OSD([sQuery(id+"F23.wireOp",EDGE,"E20.bottom"),sQuery(id+"F23.wireOp",EDGE,"E20.top"),sQuery(id+"F23.wireOp",EDGE,"E20.left"),sQuery(id+"F23.wireOp",EDGE,"E20.right")])],"isStart":true})]}),makeQuery(id+"F26.opExtrude","CAP_FACE",FACE,{"disambiguationData":[OSD([sQuery(id+"F25.wireOp",EDGE,"E21.bottom"),sQuery(id+"F25.wireOp",EDGE,"E21.top"),sQuery(id+"F25.wireOp",EDGE,"E21.left"),sQuery(id+"F25.wireOp",EDGE,"E21.right")])],"isStart":true})]}),makeQuery(id+"F28.opExtrude","CAP_FACE",FACE,{"disambiguationData":[OSD([sQuery(id+"F27.wireOp",EDGE,"E22.bottom"),sQuery(id+"F27.wireOp",EDGE,"E22.top"),sQuery(id+"F27.wireOp",EDGE,"E22.left"),sQuery(id+"F27.wireOp",EDGE,"E22.right")])],"isStart":true})]}),makeQuery(id+"F30.opExtrude","CAP_FACE",FACE,{"disambiguationData":[OSD([sQuery(id+"F29.wireOp",EDGE,"E23.bottom"),sQuery(id+"F29.wireOp",EDGE,"E23.top"),sQuery(id+"F29.wireOp",EDGE,"E23.left"),sQuery(id+"F29.wireOp",EDGE,"E23.right")])],"isStart":true})]}),makeQuery(id+"F32.opExtrude","CAP_FACE",FACE,{"disambiguationData":[OSD([sQuery(id+"F31.wireOp",EDGE,"E24.bottom"),sQuery(id+"F31.wireOp",EDGE,"E24.top"),sQuery(id+"F31.wireOp",EDGE,"E24.left"),sQuery(id+"F31.wireOp",EDGE,"E24.right"),sQuery(id+"F31.wireOp",EDGE,"E25.top"),sQuery(id+"F31.wireOp",EDGE,"E25.left"),sQuery(id+"F31.wireOp",EDGE,"E25.right"),sQuery(id+"F31.wireOp",EDGE,"E26.top"),sQuery(id+"F31.wireOp",EDGE,"E26.left"),sQuery(id+"F31.wireOp",EDGE,"E26.right")])],"isStart":true})]}),makeQuery(id+"F34.opExtrude","CAP_FACE",FACE,{"disambiguationData":[OSD([sQuery(id+"F33.wireOp",EDGE,"E27.bottom"),sQuery(id+"F33.wireOp",EDGE,"E27.top"),sQuery(id+"F33.wireOp",EDGE,"E27.left"),sQuery(id+"F33.wireOp",EDGE,"E27.right"),sQuery(id+"F33.wireOp",EDGE,"E28.bottom"),sQuery(id+"F33.wireOp",EDGE,"E28.top"),sQuery(id+"F33.wireOp",EDGE,"E29.bottom"),sQuery(id+"F33.wireOp",EDGE,"E29.top"),sQuery(id+"F33.wireOp",EDGE,"E29.left"),sQuery(id+"F33.wireOp",EDGE,"E29.right"),sQuery(id+"F33.wireOp",EDGE,"E30.bottom"),sQuery(id+"F33.wireOp",EDGE,"E30.top"),sQuery(id+"F33.wireOp",EDGE,"E31.bottom"),sQuery(id+"F33.wireOp",EDGE,"E31.top"),sQuery(id+"F33.wireOp",EDGE,"E31.left"),sQuery(id+"F33.wireOp",EDGE,"E31.right")])],"isStart":true})]}),makeQuery(id+"F36.opExtrude","CAP_FACE",FACE,{"disambiguationData":[OSD([sQuery(id+"F35.wireOp",EDGE,"E32.bottom"),sQuery(id+"F35.wireOp",EDGE,"E32.top"),sQuery(id+"F35.wireOp",EDGE,"E32.left"),sQuery(id+"F35.wireOp",EDGE,"E32.right")])],"isStart":true})]});
            var sketch = newSketch(context, id + "F37", { "sketchPlane" : qUnion([Q0])});
            skLineSegment(sketch, "E33.bottom", {"start": v(755.62, 336.55) * mm, "end": v(774.67, 336.55) * mm});
            skLineSegment(sketch, "E33.top", {"start": v(755.62, 425.45) * mm, "end": v(774.67, 425.45) * mm});
            skLineSegment(sketch, "E33.left", {"start": v(755.62, 336.55) * mm, "end": v(755.62, 425.45) * mm});
            skLineSegment(sketch, "E33.right", {"start": v(774.67, 336.55) * mm, "end": v(774.67, 425.45) * mm});
            skSolve(sketch);
        }
        {
            var Q0;
            {var subQ3=sQuery(id+"F37.wireOp",EDGE,"E33.bottom");Q0=makeQuery(id+"F37.imprint","IMPRINT",FACE,{"disambiguationData":[TD([[makeQuery(id+"F37.imprint","IMPRINT",EDGE,{"derivedFrom":subQ3}),1.0]])]});}
            extrude(context, id + "F38", {"entities" : qUnion([Q0]), "operationType" : NewBodyOperationType.ADD, "oppositeDirection" : true, "depth" : 406.4 * mm, "offsetDistance" : 25.4 * mm});
        }
        {
            var Q0;
            Q0=makeQuery(id+"F08OdCpgHM6mKrp_1.boolean.opBoolean","MERGE",FACE,{"derivedFrom":[makeQuery(id+"F38.boolean.opBoolean","MERGE",FACE,{"derivedFrom":[makeQuery(id+"F36.boolean.opBoolean","MERGE",FACE,{"derivedFrom":[makeQuery(id+"F34.boolean.opBoolean","MERGE",FACE,{"derivedFrom":[makeQuery(id+"F32.boolean.opBoolean","MERGE",FACE,{"derivedFrom":[makeQuery(id+"F30.boolean.opBoolean","MERGE",FACE,{"derivedFrom":[makeQuery(id+"F28.boolean.opBoolean","MERGE",FACE,{"derivedFrom":[makeQuery(id+"F26.boolean.opBoolean","MERGE",FACE,{"derivedFrom":[makeQuery(id+"F24.boolean.opBoolean","MERGE",FACE,{"derivedFrom":[makeQuery(id+"F22.boolean.opBoolean","MERGE",FACE,{"derivedFrom":[makeQuery(id+"F20.boolean.opBoolean","MERGE",FACE,{"derivedFrom":[makeQuery(id+"F18.boolean.opBoolean","MERGE",FACE,{"derivedFrom":[makeQuery(id+"F12.boolean.opBoolean","MERGE",FACE,{"derivedFrom":[makeQuery(id+"F10.boolean.opBoolean","MERGE",FACE,{"derivedFrom":[makeQuery(id+"F6.boolean.opBoolean","MERGE",FACE,{"derivedFrom":[makeQuery(id+"F4.boolean.opBoolean","MERGE",FACE,{"derivedFrom":[makeQuery(id+"F1.opExtrude","CAP_FACE",FACE,{"disambiguationData":[OSD([sQuery(id+"F0.wireOp",EDGE,"E0.bottom"),sQuery(id+"F0.wireOp",EDGE,"E0.top"),sQuery(id+"F0.wireOp",EDGE,"E0.left"),sQuery(id+"F0.wireOp",EDGE,"E0.right")])],"isStart":false}),makeQuery(id+"F4.opExtrude","SWEPT_FACE",FACE,{"disambiguationData":[OSD([sQuery(id+"F2.wireOp",EDGE,"E1.bottom")])]})]}),makeQuery(id+"F6.opExtrude","CAP_FACE",FACE,{"disambiguationData":[OSD([sQuery(id+"F5.wireOp",EDGE,"E2.bottom"),sQuery(id+"F5.wireOp",EDGE,"E2.top"),sQuery(id+"F5.wireOp",EDGE,"E2.left"),sQuery(id+"F5.wireOp",EDGE,"E2.right")])],"isStart":true})]}),makeQuery(id+"F10.opExtrude","SWEPT_FACE",FACE,{"disambiguationData":[OSD([sQuery(id+"F9.wireOp",EDGE,"E4.bottom")])]}),makeQuery(id+"F10.opExtrude","SWEPT_FACE",FACE,{"disambiguationData":[OSD([sQuery(id+"F9.wireOp",EDGE,"E7.bottom")])]})]}),makeQuery(id+"F12.opExtrude","SWEPT_FACE",FACE,{"disambiguationData":[OSD([sQuery(id+"F11.wireOp",EDGE,"E9.bottom")])]})]}),makeQuery(id+"F18.opExtrude","CAP_FACE",FACE,{"disambiguationData":[OSD([sQuery(id+"F17.wireOp",EDGE,"E16.bottom"),sQuery(id+"F17.wireOp",EDGE,"E16.top"),sQuery(id+"F17.wireOp",EDGE,"E16.left"),sQuery(id+"F17.wireOp",EDGE,"E16.right")])],"isStart":true})]}),makeQuery(id+"F20.opExtrude","CAP_FACE",FACE,{"disambiguationData":[OSD([sQuery(id+"F19.wireOp",EDGE,"E17.bottom"),sQuery(id+"F19.wireOp",EDGE,"E17.top"),sQuery(id+"F19.wireOp",EDGE,"E17.left"),sQuery(id+"F19.wireOp",EDGE,"E17.right")])],"isStart":true})]}),makeQuery(id+"F22.opExtrude","CAP_FACE",FACE,{"disambiguationData":[OSD([sQuery(id+"F21.wireOp",EDGE,"E18.bottom"),sQuery(id+"F21.wireOp",EDGE,"E18.top"),sQuery(id+"F21.wireOp",EDGE,"E18.left"),sQuery(id+"F21.wireOp",EDGE,"E18.right")])],"isStart":false})]}),makeQuery(id+"F24.opExtrude","CAP_FACE",FACE,{"disambiguationData":[OSD([sQuery(id+"F23.wireOp",EDGE,"E19.bottom"),sQuery(id+"F23.wireOp",EDGE,"E19.top"),sQuery(id+"F23.wireOp",EDGE,"E19.left"),sQuery(id+"F23.wireOp",EDGE,"E19.right")])],"isStart":true}),makeQuery(id+"F24.opExtrude","CAP_FACE",FACE,{"disambiguationData":[OSD([sQuery(id+"F23.wireOp",EDGE,"E20.bottom"),sQuery(id+"F23.wireOp",EDGE,"E20.top"),sQuery(id+"F23.wireOp",EDGE,"E20.left"),sQuery(id+"F23.wireOp",EDGE,"E20.right")])],"isStart":true})]}),makeQuery(id+"F26.opExtrude","CAP_FACE",FACE,{"disambiguationData":[OSD([sQuery(id+"F25.wireOp",EDGE,"E21.bottom"),sQuery(id+"F25.wireOp",EDGE,"E21.top"),sQuery(id+"F25.wireOp",EDGE,"E21.left"),sQuery(id+"F25.wireOp",EDGE,"E21.right")])],"isStart":true})]}),makeQuery(id+"F28.opExtrude","CAP_FACE",FACE,{"disambiguationData":[OSD([sQuery(id+"F27.wireOp",EDGE,"E22.bottom"),sQuery(id+"F27.wireOp",EDGE,"E22.top"),sQuery(id+"F27.wireOp",EDGE,"E22.left"),sQuery(id+"F27.wireOp",EDGE,"E22.right")])],"isStart":true})]}),makeQuery(id+"F30.opExtrude","CAP_FACE",FACE,{"disambiguationData":[OSD([sQuery(id+"F29.wireOp",EDGE,"E23.bottom"),sQuery(id+"F29.wireOp",EDGE,"E23.top"),sQuery(id+"F29.wireOp",EDGE,"E23.left"),sQuery(id+"F29.wireOp",EDGE,"E23.right")])],"isStart":true})]}),makeQuery(id+"F32.opExtrude","CAP_FACE",FACE,{"disambiguationData":[OSD([sQuery(id+"F31.wireOp",EDGE,"E24.bottom"),sQuery(id+"F31.wireOp",EDGE,"E24.top"),sQuery(id+"F31.wireOp",EDGE,"E24.left"),sQuery(id+"F31.wireOp",EDGE,"E24.right"),sQuery(id+"F31.wireOp",EDGE,"E25.top"),sQuery(id+"F31.wireOp",EDGE,"E25.left"),sQuery(id+"F31.wireOp",EDGE,"E25.right"),sQuery(id+"F31.wireOp",EDGE,"E26.top"),sQuery(id+"F31.wireOp",EDGE,"E26.left"),sQuery(id+"F31.wireOp",EDGE,"E26.right")])],"isStart":true})]}),makeQuery(id+"F34.opExtrude","CAP_FACE",FACE,{"disambiguationData":[OSD([sQuery(id+"F33.wireOp",EDGE,"E27.bottom"),sQuery(id+"F33.wireOp",EDGE,"E27.top"),sQuery(id+"F33.wireOp",EDGE,"E27.left"),sQuery(id+"F33.wireOp",EDGE,"E27.right"),sQuery(id+"F33.wireOp",EDGE,"E28.bottom"),sQuery(id+"F33.wireOp",EDGE,"E28.top"),sQuery(id+"F33.wireOp",EDGE,"E29.bottom"),sQuery(id+"F33.wireOp",EDGE,"E29.top"),sQuery(id+"F33.wireOp",EDGE,"E29.left"),sQuery(id+"F33.wireOp",EDGE,"E29.right"),sQuery(id+"F33.wireOp",EDGE,"E30.bottom"),sQuery(id+"F33.wireOp",EDGE,"E30.top"),sQuery(id+"F33.wireOp",EDGE,"E31.bottom"),sQuery(id+"F33.wireOp",EDGE,"E31.top"),sQuery(id+"F33.wireOp",EDGE,"E31.left"),sQuery(id+"F33.wireOp",EDGE,"E31.right")])],"isStart":true})]}),makeQuery(id+"F36.opExtrude","CAP_FACE",FACE,{"disambiguationData":[OSD([sQuery(id+"F35.wireOp",EDGE,"E32.bottom"),sQuery(id+"F35.wireOp",EDGE,"E32.top"),sQuery(id+"F35.wireOp",EDGE,"E32.left"),sQuery(id+"F35.wireOp",EDGE,"E32.right")])],"isStart":true})]}),makeQuery(id+"F38.opExtrude","CAP_FACE",FACE,{"disambiguationData":[OSD([sQuery(id+"F37.wireOp",EDGE,"E33.bottom"),sQuery(id+"F37.wireOp",EDGE,"E33.top"),sQuery(id+"F37.wireOp",EDGE,"E33.left"),sQuery(id+"F37.wireOp",EDGE,"E33.right")])],"isStart":true})]}),makeQuery(id+"F08OdCpgHM6mKrp_1.opExtrude","SWEPT_FACE",FACE,{"disambiguationData":[OSD([sQuery(id+"FjyFJpoyjPrBSSn_1.wireOp",EDGE,"967be1a8-157c-42f3-94d2-f701a76993c1.bottom")])]})]});
            var sketch = newSketch(context, id + "F39", { "sketchPlane" : qUnion([Q0])});
            skLineSegment(sketch, "E34.bottom", {"start": v(774.67, -57.15) * mm, "end": v(685.77, -57.15) * mm});
            skLineSegment(sketch, "E34.top", {"start": v(774.67, -76.2) * mm, "end": v(685.77, -76.2) * mm});
            skLineSegment(sketch, "E34.left", {"start": v(774.67, -57.15) * mm, "end": v(774.67, -76.2) * mm});
            skLineSegment(sketch, "E34.right", {"start": v(685.77, -57.15) * mm, "end": v(685.77, -76.2) * mm});
            skSolve(sketch);
        }
        {
            var Q0;
            Q0=makeQuery(id+"F39.imprint","IMPRINT",FACE,{"disambiguationData":[TD([[makeQuery(id+"F39.imprint","IMPRINT",EDGE,{"derivedFrom":sQuery(id+"F39.wireOp",EDGE,"E34.top")}),-1.0]])]});
            extrude(context, id + "F40", {"entities" : qUnion([Q0]), "operationType" : NewBodyOperationType.ADD, "oppositeDirection" : true, "depth" : 863.6 * mm, "offsetDistance" : 25.4 * mm});
        }
        {
            var Q0;
            Q0=makeQuery(id+"F38.opExtrude","SWEPT_FACE",FACE,{"disambiguationData":[OSD([sQuery(id+"F37.wireOp",EDGE,"E33.bottom")])]});
            var sketch = newSketch(context, id + "F41", { "sketchPlane" : qUnion([Q0])});
            skLineSegment(sketch, "E35.bottom", {"start": v(755.62, 406.4) * mm, "end": v(774.65, 406.4) * mm});
            skLineSegment(sketch, "E35.top", {"start": v(755.62, 317.5) * mm, "end": v(774.65, 317.5) * mm});
            skLineSegment(sketch, "E35.left", {"start": v(755.62, 406.4) * mm, "end": v(755.62, 317.5) * mm});
            skLineSegment(sketch, "E35.right", {"start": v(774.65, 406.4) * mm, "end": v(774.65, 317.5) * mm});
            skLineSegment(sketch, "E36.bottom", {"start": v(755.62, 0) * mm, "end": v(774.65, 0) * mm});
            skLineSegment(sketch, "E36.top", {"start": v(755.62, 88.9) * mm, "end": v(774.65, 88.9) * mm});
            skLineSegment(sketch, "E36.left", {"start": v(755.62, 0) * mm, "end": v(755.62, 88.9) * mm});
            skLineSegment(sketch, "E36.right", {"start": v(774.65, 0) * mm, "end": v(774.65, 88.9) * mm});
            skSolve(sketch);
        }
        {
            var Q0;
            Q0=makeQuery(id+"F41.imprint","IMPRINT",FACE,{"disambiguationData":[TD([[makeQuery(id+"F41.imprint","IMPRINT",EDGE,{"derivedFrom":sQuery(id+"F41.wireOp",EDGE,"E36.bottom")}),1.0]])]});
            var Q1;
            Q1=makeQuery(id+"F41.imprint","IMPRINT",FACE,{"disambiguationData":[TD([[makeQuery(id+"F41.imprint","IMPRINT",EDGE,{"derivedFrom":sQuery(id+"F41.wireOp",EDGE,"E35.bottom")}),-1.0]])]});
            extrude(context, id + "F42", {"entities" : qUnion([Q0, Q1]), "operationType" : NewBodyOperationType.ADD, "depth" : 304.8 * mm, "offsetDistance" : 25.4 * mm});
        }
        {
            var Q0;
            Q0=makeQuery(id+"F42.boolean.opBoolean","MERGE",FACE,{"derivedFrom":[makeQuery(id+"F40.boolean.opBoolean","MERGE",FACE,{"derivedFrom":[makeQuery(id+"F38.boolean.opBoolean","MERGE",FACE,{"derivedFrom":[makeQuery(id+"F36.boolean.opBoolean","MERGE",FACE,{"derivedFrom":[makeQuery(id+"F34.boolean.opBoolean","MERGE",FACE,{"derivedFrom":[makeQuery(id+"F32.boolean.opBoolean","MERGE",FACE,{"derivedFrom":[makeQuery(id+"F30.boolean.opBoolean","MERGE",FACE,{"derivedFrom":[makeQuery(id+"F28.boolean.opBoolean","MERGE",FACE,{"derivedFrom":[makeQuery(id+"F26.boolean.opBoolean","MERGE",FACE,{"derivedFrom":[makeQuery(id+"F24.boolean.opBoolean","MERGE",FACE,{"derivedFrom":[makeQuery(id+"F22.boolean.opBoolean","MERGE",FACE,{"derivedFrom":[makeQuery(id+"F20.boolean.opBoolean","MERGE",FACE,{"derivedFrom":[makeQuery(id+"F18.boolean.opBoolean","MERGE",FACE,{"derivedFrom":[makeQuery(id+"F12.boolean.opBoolean","MERGE",FACE,{"derivedFrom":[makeQuery(id+"F10.boolean.opBoolean","MERGE",FACE,{"derivedFrom":[makeQuery(id+"F6.boolean.opBoolean","MERGE",FACE,{"derivedFrom":[makeQuery(id+"F4.boolean.opBoolean","MERGE",FACE,{"derivedFrom":[makeQuery(id+"F1.opExtrude","CAP_FACE",FACE,{"disambiguationData":[OSD([sQuery(id+"F0.wireOp",EDGE,"E0.bottom"),sQuery(id+"F0.wireOp",EDGE,"E0.top"),sQuery(id+"F0.wireOp",EDGE,"E0.left"),sQuery(id+"F0.wireOp",EDGE,"E0.right")])],"isStart":false}),makeQuery(id+"F4.opExtrude","SWEPT_FACE",FACE,{"disambiguationData":[OSD([sQuery(id+"F2.wireOp",EDGE,"E1.bottom")])]})]}),makeQuery(id+"F6.opExtrude","CAP_FACE",FACE,{"disambiguationData":[OSD([sQuery(id+"F5.wireOp",EDGE,"E2.bottom"),sQuery(id+"F5.wireOp",EDGE,"E2.top"),sQuery(id+"F5.wireOp",EDGE,"E2.left"),sQuery(id+"F5.wireOp",EDGE,"E2.right")])],"isStart":true})]}),makeQuery(id+"F10.opExtrude","SWEPT_FACE",FACE,{"disambiguationData":[OSD([sQuery(id+"F9.wireOp",EDGE,"E4.bottom")])]}),makeQuery(id+"F10.opExtrude","SWEPT_FACE",FACE,{"disambiguationData":[OSD([sQuery(id+"F9.wireOp",EDGE,"E7.bottom")])]})]}),makeQuery(id+"F12.opExtrude","SWEPT_FACE",FACE,{"disambiguationData":[OSD([sQuery(id+"F11.wireOp",EDGE,"E9.bottom")])]})]}),makeQuery(id+"F18.opExtrude","CAP_FACE",FACE,{"disambiguationData":[OSD([sQuery(id+"F17.wireOp",EDGE,"E16.bottom"),sQuery(id+"F17.wireOp",EDGE,"E16.top"),sQuery(id+"F17.wireOp",EDGE,"E16.left"),sQuery(id+"F17.wireOp",EDGE,"E16.right")])],"isStart":true})]}),makeQuery(id+"F20.opExtrude","CAP_FACE",FACE,{"disambiguationData":[OSD([sQuery(id+"F19.wireOp",EDGE,"E17.bottom"),sQuery(id+"F19.wireOp",EDGE,"E17.top"),sQuery(id+"F19.wireOp",EDGE,"E17.left"),sQuery(id+"F19.wireOp",EDGE,"E17.right")])],"isStart":true})]}),makeQuery(id+"F22.opExtrude","CAP_FACE",FACE,{"disambiguationData":[OSD([sQuery(id+"F21.wireOp",EDGE,"E18.bottom"),sQuery(id+"F21.wireOp",EDGE,"E18.top"),sQuery(id+"F21.wireOp",EDGE,"E18.left"),sQuery(id+"F21.wireOp",EDGE,"E18.right")])],"isStart":false})]}),makeQuery(id+"F24.opExtrude","CAP_FACE",FACE,{"disambiguationData":[OSD([sQuery(id+"F23.wireOp",EDGE,"E19.bottom"),sQuery(id+"F23.wireOp",EDGE,"E19.top"),sQuery(id+"F23.wireOp",EDGE,"E19.left"),sQuery(id+"F23.wireOp",EDGE,"E19.right")])],"isStart":true}),makeQuery(id+"F24.opExtrude","CAP_FACE",FACE,{"disambiguationData":[OSD([sQuery(id+"F23.wireOp",EDGE,"E20.bottom"),sQuery(id+"F23.wireOp",EDGE,"E20.top"),sQuery(id+"F23.wireOp",EDGE,"E20.left"),sQuery(id+"F23.wireOp",EDGE,"E20.right")])],"isStart":true})]}),makeQuery(id+"F26.opExtrude","CAP_FACE",FACE,{"disambiguationData":[OSD([sQuery(id+"F25.wireOp",EDGE,"E21.bottom"),sQuery(id+"F25.wireOp",EDGE,"E21.top"),sQuery(id+"F25.wireOp",EDGE,"E21.left"),sQuery(id+"F25.wireOp",EDGE,"E21.right")])],"isStart":true})]}),makeQuery(id+"F28.opExtrude","CAP_FACE",FACE,{"disambiguationData":[OSD([sQuery(id+"F27.wireOp",EDGE,"E22.bottom"),sQuery(id+"F27.wireOp",EDGE,"E22.top"),sQuery(id+"F27.wireOp",EDGE,"E22.left"),sQuery(id+"F27.wireOp",EDGE,"E22.right")])],"isStart":true})]}),makeQuery(id+"F30.opExtrude","CAP_FACE",FACE,{"disambiguationData":[OSD([sQuery(id+"F29.wireOp",EDGE,"E23.bottom"),sQuery(id+"F29.wireOp",EDGE,"E23.top"),sQuery(id+"F29.wireOp",EDGE,"E23.left"),sQuery(id+"F29.wireOp",EDGE,"E23.right")])],"isStart":true})]}),makeQuery(id+"F32.opExtrude","CAP_FACE",FACE,{"disambiguationData":[OSD([sQuery(id+"F31.wireOp",EDGE,"E24.bottom"),sQuery(id+"F31.wireOp",EDGE,"E24.top"),sQuery(id+"F31.wireOp",EDGE,"E24.left"),sQuery(id+"F31.wireOp",EDGE,"E24.right"),sQuery(id+"F31.wireOp",EDGE,"E25.top"),sQuery(id+"F31.wireOp",EDGE,"E25.left"),sQuery(id+"F31.wireOp",EDGE,"E25.right"),sQuery(id+"F31.wireOp",EDGE,"E26.top"),sQuery(id+"F31.wireOp",EDGE,"E26.left"),sQuery(id+"F31.wireOp",EDGE,"E26.right")])],"isStart":true})]}),makeQuery(id+"F34.opExtrude","CAP_FACE",FACE,{"disambiguationData":[OSD([sQuery(id+"F33.wireOp",EDGE,"E27.bottom"),sQuery(id+"F33.wireOp",EDGE,"E27.top"),sQuery(id+"F33.wireOp",EDGE,"E27.left"),sQuery(id+"F33.wireOp",EDGE,"E27.right"),sQuery(id+"F33.wireOp",EDGE,"E28.bottom"),sQuery(id+"F33.wireOp",EDGE,"E28.top"),sQuery(id+"F33.wireOp",EDGE,"E29.bottom"),sQuery(id+"F33.wireOp",EDGE,"E29.top"),sQuery(id+"F33.wireOp",EDGE,"E29.left"),sQuery(id+"F33.wireOp",EDGE,"E29.right"),sQuery(id+"F33.wireOp",EDGE,"E30.bottom"),sQuery(id+"F33.wireOp",EDGE,"E30.top"),sQuery(id+"F33.wireOp",EDGE,"E31.bottom"),sQuery(id+"F33.wireOp",EDGE,"E31.top"),sQuery(id+"F33.wireOp",EDGE,"E31.left"),sQuery(id+"F33.wireOp",EDGE,"E31.right")])],"isStart":true})]}),makeQuery(id+"F36.opExtrude","CAP_FACE",FACE,{"disambiguationData":[OSD([sQuery(id+"F35.wireOp",EDGE,"E32.bottom"),sQuery(id+"F35.wireOp",EDGE,"E32.top"),sQuery(id+"F35.wireOp",EDGE,"E32.left"),sQuery(id+"F35.wireOp",EDGE,"E32.right")])],"isStart":true})]}),makeQuery(id+"F38.opExtrude","CAP_FACE",FACE,{"disambiguationData":[OSD([sQuery(id+"F37.wireOp",EDGE,"E33.bottom"),sQuery(id+"F37.wireOp",EDGE,"E33.top"),sQuery(id+"F37.wireOp",EDGE,"E33.left"),sQuery(id+"F37.wireOp",EDGE,"E33.right")])],"isStart":true})]}),makeQuery(id+"F40.opExtrude","CAP_FACE",FACE,{"disambiguationData":[OSD([sQuery(id+"F39.wireOp",EDGE,"E34.bottom"),sQuery(id+"F39.wireOp",EDGE,"E34.top"),sQuery(id+"F39.wireOp",EDGE,"E34.left"),sQuery(id+"F39.wireOp",EDGE,"E34.right")])],"isStart":true})]}),makeQuery(id+"F42.opExtrude","SWEPT_FACE",FACE,{"disambiguationData":[OSD([sQuery(id+"F41.wireOp",EDGE,"E35.bottom")])]})]});
            var sketch = newSketch(context, id + "F43", { "sketchPlane" : qUnion([Q0])});
            skLineSegment(sketch, "E37.bottom", {"start": v(-19.02, 31.75) * mm, "end": v(-38.07, 31.75) * mm});
            skLineSegment(sketch, "E37.top", {"start": v(-19.02, -57.15) * mm, "end": v(-38.07, -57.15) * mm});
            skLineSegment(sketch, "E37.left", {"start": v(-19.02, 31.75) * mm, "end": v(-19.02, -57.15) * mm});
            skLineSegment(sketch, "E37.right", {"start": v(-38.07, 31.75) * mm, "end": v(-38.07, -57.15) * mm});
            skLineSegment(sketch, "E38.bottom", {"start": v(-19.02, 336.55) * mm, "end": v(-38.07, 336.55) * mm});
            skLineSegment(sketch, "E38.top", {"start": v(-19.02, 425.45) * mm, "end": v(-38.07, 425.45) * mm});
            skLineSegment(sketch, "E38.left", {"start": v(-19.02, 336.55) * mm, "end": v(-19.02, 425.45) * mm});
            skLineSegment(sketch, "E38.right", {"start": v(-38.07, 336.55) * mm, "end": v(-38.07, 425.45) * mm});
            skSolve(sketch);
        }
        {
            var Q0;
            {var subQ2=sQuery(id+"F43.wireOp",EDGE,"E37.bottom");Q0=makeQuery(id+"F43.imprint","IMPRINT",FACE,{"disambiguationData":[TD([[makeQuery(id+"F43.imprint","IMPRINT",EDGE,{"derivedFrom":subQ2}),1.0]])]});}
            var Q1;
            {var subQ3=sQuery(id+"F43.wireOp",EDGE,"E38.bottom");Q1=makeQuery(id+"F43.imprint","IMPRINT",FACE,{"disambiguationData":[TD([[makeQuery(id+"F43.imprint","IMPRINT",EDGE,{"derivedFrom":subQ3}),-1.0]])]});}
            extrude(context, id + "F44", {"entities" : qUnion([Q0, Q1]), "operationType" : NewBodyOperationType.ADD, "oppositeDirection" : true, "depth" : 406.4 * mm, "offsetDistance" : 25.4 * mm});
        }
        {
            var Q0;
            Q0=makeQuery(id+"F44.opExtrude","SWEPT_FACE",FACE,{"disambiguationData":[OSD([sQuery(id+"F43.wireOp",EDGE,"E37.bottom")])]});
            var sketch = newSketch(context, id + "F45", { "sketchPlane" : qUnion([Q0])});
            skLineSegment(sketch, "E39.bottom", {"start": v(19.02, 406.4) * mm, "end": v(38.05, 406.4) * mm});
            skLineSegment(sketch, "E39.top", {"start": v(19.02, 317.5) * mm, "end": v(38.05, 317.5) * mm});
            skLineSegment(sketch, "E39.left", {"start": v(19.02, 406.4) * mm, "end": v(19.02, 317.5) * mm});
            skLineSegment(sketch, "E39.right", {"start": v(38.05, 406.4) * mm, "end": v(38.05, 317.5) * mm});
            skLineSegment(sketch, "E40.bottom", {"start": v(19.02, 0) * mm, "end": v(38.05, 0) * mm});
            skLineSegment(sketch, "E40.top", {"start": v(19.02, 88.9) * mm, "end": v(38.05, 88.9) * mm});
            skLineSegment(sketch, "E40.left", {"start": v(19.02, 0) * mm, "end": v(19.02, 88.9) * mm});
            skLineSegment(sketch, "E40.right", {"start": v(38.05, 0) * mm, "end": v(38.05, 88.9) * mm});
            skSolve(sketch);
        }
        {
            var Q0;
            Q0=makeQuery(id+"F45.imprint","IMPRINT",FACE,{"disambiguationData":[TD([[makeQuery(id+"F45.imprint","IMPRINT",EDGE,{"derivedFrom":sQuery(id+"F45.wireOp",EDGE,"E40.bottom")}),1.0]])]});
            var Q1;
            Q1=makeQuery(id+"F45.imprint","IMPRINT",FACE,{"disambiguationData":[TD([[makeQuery(id+"F45.imprint","IMPRINT",EDGE,{"derivedFrom":sQuery(id+"F45.wireOp",EDGE,"E39.bottom")}),-1.0]])]});
            extrude(context, id + "F46", {"entities" : qUnion([Q0, Q1]), "operationType" : NewBodyOperationType.ADD, "depth" : 304.8 * mm, "offsetDistance" : 25.4 * mm});
        }
        {
            var Q0;
            Q0=makeQuery(id+"F46.boolean.opBoolean","MERGE",FACE,{"derivedFrom":[makeQuery(id+"F44.boolean.opBoolean","MERGE",FACE,{"derivedFrom":[makeQuery(id+"F42.boolean.opBoolean","MERGE",FACE,{"derivedFrom":[makeQuery(id+"F40.boolean.opBoolean","MERGE",FACE,{"derivedFrom":[makeQuery(id+"F38.boolean.opBoolean","MERGE",FACE,{"derivedFrom":[makeQuery(id+"F36.boolean.opBoolean","MERGE",FACE,{"derivedFrom":[makeQuery(id+"F34.boolean.opBoolean","MERGE",FACE,{"derivedFrom":[makeQuery(id+"F32.boolean.opBoolean","MERGE",FACE,{"derivedFrom":[makeQuery(id+"F30.boolean.opBoolean","MERGE",FACE,{"derivedFrom":[makeQuery(id+"F28.boolean.opBoolean","MERGE",FACE,{"derivedFrom":[makeQuery(id+"F26.boolean.opBoolean","MERGE",FACE,{"derivedFrom":[makeQuery(id+"F24.boolean.opBoolean","MERGE",FACE,{"derivedFrom":[makeQuery(id+"F22.boolean.opBoolean","MERGE",FACE,{"derivedFrom":[makeQuery(id+"F20.boolean.opBoolean","MERGE",FACE,{"derivedFrom":[makeQuery(id+"F18.boolean.opBoolean","MERGE",FACE,{"derivedFrom":[makeQuery(id+"F12.boolean.opBoolean","MERGE",FACE,{"derivedFrom":[makeQuery(id+"F10.boolean.opBoolean","MERGE",FACE,{"derivedFrom":[makeQuery(id+"F6.boolean.opBoolean","MERGE",FACE,{"derivedFrom":[makeQuery(id+"F4.boolean.opBoolean","MERGE",FACE,{"derivedFrom":[makeQuery(id+"F1.opExtrude","CAP_FACE",FACE,{"disambiguationData":[OSD([sQuery(id+"F0.wireOp",EDGE,"E0.bottom"),sQuery(id+"F0.wireOp",EDGE,"E0.top"),sQuery(id+"F0.wireOp",EDGE,"E0.left"),sQuery(id+"F0.wireOp",EDGE,"E0.right")])],"isStart":false}),makeQuery(id+"F4.opExtrude","SWEPT_FACE",FACE,{"disambiguationData":[OSD([sQuery(id+"F2.wireOp",EDGE,"E1.bottom")])]})]}),makeQuery(id+"F6.opExtrude","CAP_FACE",FACE,{"disambiguationData":[OSD([sQuery(id+"F5.wireOp",EDGE,"E2.bottom"),sQuery(id+"F5.wireOp",EDGE,"E2.top"),sQuery(id+"F5.wireOp",EDGE,"E2.left"),sQuery(id+"F5.wireOp",EDGE,"E2.right")])],"isStart":true})]}),makeQuery(id+"F10.opExtrude","SWEPT_FACE",FACE,{"disambiguationData":[OSD([sQuery(id+"F9.wireOp",EDGE,"E4.bottom")])]}),makeQuery(id+"F10.opExtrude","SWEPT_FACE",FACE,{"disambiguationData":[OSD([sQuery(id+"F9.wireOp",EDGE,"E7.bottom")])]})]}),makeQuery(id+"F12.opExtrude","SWEPT_FACE",FACE,{"disambiguationData":[OSD([sQuery(id+"F11.wireOp",EDGE,"E9.bottom")])]})]}),makeQuery(id+"F18.opExtrude","CAP_FACE",FACE,{"disambiguationData":[OSD([sQuery(id+"F17.wireOp",EDGE,"E16.bottom"),sQuery(id+"F17.wireOp",EDGE,"E16.top"),sQuery(id+"F17.wireOp",EDGE,"E16.left"),sQuery(id+"F17.wireOp",EDGE,"E16.right")])],"isStart":true})]}),makeQuery(id+"F20.opExtrude","CAP_FACE",FACE,{"disambiguationData":[OSD([sQuery(id+"F19.wireOp",EDGE,"E17.bottom"),sQuery(id+"F19.wireOp",EDGE,"E17.top"),sQuery(id+"F19.wireOp",EDGE,"E17.left"),sQuery(id+"F19.wireOp",EDGE,"E17.right")])],"isStart":true})]}),makeQuery(id+"F22.opExtrude","CAP_FACE",FACE,{"disambiguationData":[OSD([sQuery(id+"F21.wireOp",EDGE,"E18.bottom"),sQuery(id+"F21.wireOp",EDGE,"E18.top"),sQuery(id+"F21.wireOp",EDGE,"E18.left"),sQuery(id+"F21.wireOp",EDGE,"E18.right")])],"isStart":false})]}),makeQuery(id+"F24.opExtrude","CAP_FACE",FACE,{"disambiguationData":[OSD([sQuery(id+"F23.wireOp",EDGE,"E19.bottom"),sQuery(id+"F23.wireOp",EDGE,"E19.top"),sQuery(id+"F23.wireOp",EDGE,"E19.left"),sQuery(id+"F23.wireOp",EDGE,"E19.right")])],"isStart":true}),makeQuery(id+"F24.opExtrude","CAP_FACE",FACE,{"disambiguationData":[OSD([sQuery(id+"F23.wireOp",EDGE,"E20.bottom"),sQuery(id+"F23.wireOp",EDGE,"E20.top"),sQuery(id+"F23.wireOp",EDGE,"E20.left"),sQuery(id+"F23.wireOp",EDGE,"E20.right")])],"isStart":true})]}),makeQuery(id+"F26.opExtrude","CAP_FACE",FACE,{"disambiguationData":[OSD([sQuery(id+"F25.wireOp",EDGE,"E21.bottom"),sQuery(id+"F25.wireOp",EDGE,"E21.top"),sQuery(id+"F25.wireOp",EDGE,"E21.left"),sQuery(id+"F25.wireOp",EDGE,"E21.right")])],"isStart":true})]}),makeQuery(id+"F28.opExtrude","CAP_FACE",FACE,{"disambiguationData":[OSD([sQuery(id+"F27.wireOp",EDGE,"E22.bottom"),sQuery(id+"F27.wireOp",EDGE,"E22.top"),sQuery(id+"F27.wireOp",EDGE,"E22.left"),sQuery(id+"F27.wireOp",EDGE,"E22.right")])],"isStart":true})]}),makeQuery(id+"F30.opExtrude","CAP_FACE",FACE,{"disambiguationData":[OSD([sQuery(id+"F29.wireOp",EDGE,"E23.bottom"),sQuery(id+"F29.wireOp",EDGE,"E23.top"),sQuery(id+"F29.wireOp",EDGE,"E23.left"),sQuery(id+"F29.wireOp",EDGE,"E23.right")])],"isStart":true})]}),makeQuery(id+"F32.opExtrude","CAP_FACE",FACE,{"disambiguationData":[OSD([sQuery(id+"F31.wireOp",EDGE,"E24.bottom"),sQuery(id+"F31.wireOp",EDGE,"E24.top"),sQuery(id+"F31.wireOp",EDGE,"E24.left"),sQuery(id+"F31.wireOp",EDGE,"E24.right"),sQuery(id+"F31.wireOp",EDGE,"E25.top"),sQuery(id+"F31.wireOp",EDGE,"E25.left"),sQuery(id+"F31.wireOp",EDGE,"E25.right"),sQuery(id+"F31.wireOp",EDGE,"E26.top"),sQuery(id+"F31.wireOp",EDGE,"E26.left"),sQuery(id+"F31.wireOp",EDGE,"E26.right")])],"isStart":true})]}),makeQuery(id+"F34.opExtrude","CAP_FACE",FACE,{"disambiguationData":[OSD([sQuery(id+"F33.wireOp",EDGE,"E27.bottom"),sQuery(id+"F33.wireOp",EDGE,"E27.top"),sQuery(id+"F33.wireOp",EDGE,"E27.left"),sQuery(id+"F33.wireOp",EDGE,"E27.right"),sQuery(id+"F33.wireOp",EDGE,"E28.bottom"),sQuery(id+"F33.wireOp",EDGE,"E28.top"),sQuery(id+"F33.wireOp",EDGE,"E29.bottom"),sQuery(id+"F33.wireOp",EDGE,"E29.top"),sQuery(id+"F33.wireOp",EDGE,"E29.left"),sQuery(id+"F33.wireOp",EDGE,"E29.right"),sQuery(id+"F33.wireOp",EDGE,"E30.bottom"),sQuery(id+"F33.wireOp",EDGE,"E30.top"),sQuery(id+"F33.wireOp",EDGE,"E31.bottom"),sQuery(id+"F33.wireOp",EDGE,"E31.top"),sQuery(id+"F33.wireOp",EDGE,"E31.left"),sQuery(id+"F33.wireOp",EDGE,"E31.right")])],"isStart":true})]}),makeQuery(id+"F36.opExtrude","CAP_FACE",FACE,{"disambiguationData":[OSD([sQuery(id+"F35.wireOp",EDGE,"E32.bottom"),sQuery(id+"F35.wireOp",EDGE,"E32.top"),sQuery(id+"F35.wireOp",EDGE,"E32.left"),sQuery(id+"F35.wireOp",EDGE,"E32.right")])],"isStart":true})]}),makeQuery(id+"F38.opExtrude","CAP_FACE",FACE,{"disambiguationData":[OSD([sQuery(id+"F37.wireOp",EDGE,"E33.bottom"),sQuery(id+"F37.wireOp",EDGE,"E33.top"),sQuery(id+"F37.wireOp",EDGE,"E33.left"),sQuery(id+"F37.wireOp",EDGE,"E33.right")])],"isStart":true})]}),makeQuery(id+"F40.opExtrude","CAP_FACE",FACE,{"disambiguationData":[OSD([sQuery(id+"F39.wireOp",EDGE,"E34.bottom"),sQuery(id+"F39.wireOp",EDGE,"E34.top"),sQuery(id+"F39.wireOp",EDGE,"E34.left"),sQuery(id+"F39.wireOp",EDGE,"E34.right")])],"isStart":true})]}),makeQuery(id+"F42.opExtrude","SWEPT_FACE",FACE,{"disambiguationData":[OSD([sQuery(id+"F41.wireOp",EDGE,"E35.bottom")])]})]}),makeQuery(id+"F44.opExtrude","CAP_FACE",FACE,{"disambiguationData":[OSD([sQuery(id+"F43.wireOp",EDGE,"E37.bottom"),sQuery(id+"F43.wireOp",EDGE,"E37.top"),sQuery(id+"F43.wireOp",EDGE,"E37.left"),sQuery(id+"F43.wireOp",EDGE,"E37.right")])],"isStart":true}),makeQuery(id+"F44.opExtrude","CAP_FACE",FACE,{"disambiguationData":[OSD([sQuery(id+"F43.wireOp",EDGE,"E38.bottom"),sQuery(id+"F43.wireOp",EDGE,"E38.top"),sQuery(id+"F43.wireOp",EDGE,"E38.left"),sQuery(id+"F43.wireOp",EDGE,"E38.right")])],"isStart":true})]}),makeQuery(id+"F46.opExtrude","SWEPT_FACE",FACE,{"disambiguationData":[OSD([sQuery(id+"F45.wireOp",EDGE,"E39.bottom")])]})]});
            var sketch = newSketch(context, id + "F47", { "sketchPlane" : qUnion([Q0])});
            skLineSegment(sketch, "E41.bottom", {"start": v(-38.07, -57.15) * mm, "end": v(50.83, -57.15) * mm});
            skLineSegment(sketch, "E41.top", {"start": v(-38.07, -76.2) * mm, "end": v(50.83, -76.2) * mm});
            skLineSegment(sketch, "E41.left", {"start": v(-38.07, -57.15) * mm, "end": v(-38.07, -76.2) * mm});
            skLineSegment(sketch, "E41.right", {"start": v(50.83, -57.15) * mm, "end": v(50.83, -76.2) * mm});
            skSolve(sketch);
        }
        {
            var Q0;
            Q0=makeQuery(id+"F47.imprint","IMPRINT",FACE,{"disambiguationData":[TD([[makeQuery(id+"F47.imprint","IMPRINT",EDGE,{"derivedFrom":sQuery(id+"F47.wireOp",EDGE,"E41.top")}),1.0]])]});
            extrude(context, id + "F48", {"entities" : qUnion([Q0]), "operationType" : NewBodyOperationType.ADD, "oppositeDirection" : true, "depth" : 863.6 * mm, "offsetDistance" : 25.4 * mm});
        }
        {
            var Q0;
            Q0=makeQuery(id+"F48.opExtrude","SWEPT_FACE",FACE,{"disambiguationData":[OSD([sQuery(id+"F47.wireOp",EDGE,"E41.right")])]});
            var sketch = newSketch(context, id + "F49", { "sketchPlane" : qUnion([Q0])});
            skLineSegment(sketch, "E42.bottom", {"start": v(-57.15, 406.4) * mm, "end": v(-76.17, 406.4) * mm});
            skLineSegment(sketch, "E42.top", {"start": v(-57.15, 317.5) * mm, "end": v(-76.17, 317.5) * mm});
            skLineSegment(sketch, "E42.left", {"start": v(-57.15, 406.4) * mm, "end": v(-57.15, 317.5) * mm});
            skLineSegment(sketch, "E42.right", {"start": v(-76.17, 406.4) * mm, "end": v(-76.17, 317.5) * mm});
            skLineSegment(sketch, "E43.bottom", {"start": v(-57.15, 0) * mm, "end": v(-76.17, 0) * mm});
            skLineSegment(sketch, "E43.top", {"start": v(-57.15, 88.9) * mm, "end": v(-76.17, 88.9) * mm});
            skLineSegment(sketch, "E43.left", {"start": v(-57.15, 0) * mm, "end": v(-57.15, 88.9) * mm});
            skLineSegment(sketch, "E43.right", {"start": v(-76.17, 0) * mm, "end": v(-76.17, 88.9) * mm});
            skSolve(sketch);
        }
        {
            var Q0;
            Q0=makeQuery(id+"F49.imprint","IMPRINT",FACE,{"disambiguationData":[TD([[makeQuery(id+"F49.imprint","IMPRINT",EDGE,{"derivedFrom":sQuery(id+"F49.wireOp",EDGE,"E43.bottom")}),-1.0]])]});
            var Q1;
            Q1=makeQuery(id+"F49.imprint","IMPRINT",FACE,{"disambiguationData":[TD([[makeQuery(id+"F49.imprint","IMPRINT",EDGE,{"derivedFrom":sQuery(id+"F49.wireOp",EDGE,"E42.bottom")}),1.0]])]});
            extrude(context, id + "F50", {"entities" : qUnion([Q0, Q1]), "operationType" : NewBodyOperationType.ADD, "endBound" : BoundingType.UP_TO_NEXT, "depth" : 25.4 * mm, "offsetDistance" : 25.4 * mm});
        }
        {
            var Q0;
            Q0=makeQuery(id+"F50.boolean.opBoolean","MERGE",FACE,{"derivedFrom":[makeQuery(id+"F48.boolean.opBoolean","MERGE",FACE,{"derivedFrom":[makeQuery(id+"F46.boolean.opBoolean","MERGE",FACE,{"derivedFrom":[makeQuery(id+"F44.boolean.opBoolean","MERGE",FACE,{"derivedFrom":[makeQuery(id+"F42.boolean.opBoolean","MERGE",FACE,{"derivedFrom":[makeQuery(id+"F40.boolean.opBoolean","MERGE",FACE,{"derivedFrom":[makeQuery(id+"F38.boolean.opBoolean","MERGE",FACE,{"derivedFrom":[makeQuery(id+"F36.boolean.opBoolean","MERGE",FACE,{"derivedFrom":[makeQuery(id+"F34.boolean.opBoolean","MERGE",FACE,{"derivedFrom":[makeQuery(id+"F32.boolean.opBoolean","MERGE",FACE,{"derivedFrom":[makeQuery(id+"F30.boolean.opBoolean","MERGE",FACE,{"derivedFrom":[makeQuery(id+"F28.boolean.opBoolean","MERGE",FACE,{"derivedFrom":[makeQuery(id+"F26.boolean.opBoolean","MERGE",FACE,{"derivedFrom":[makeQuery(id+"F24.boolean.opBoolean","MERGE",FACE,{"derivedFrom":[makeQuery(id+"F22.boolean.opBoolean","MERGE",FACE,{"derivedFrom":[makeQuery(id+"F20.boolean.opBoolean","MERGE",FACE,{"derivedFrom":[makeQuery(id+"F18.boolean.opBoolean","MERGE",FACE,{"derivedFrom":[makeQuery(id+"F12.boolean.opBoolean","MERGE",FACE,{"derivedFrom":[makeQuery(id+"F10.boolean.opBoolean","MERGE",FACE,{"derivedFrom":[makeQuery(id+"F6.boolean.opBoolean","MERGE",FACE,{"derivedFrom":[makeQuery(id+"F4.boolean.opBoolean","MERGE",FACE,{"derivedFrom":[makeQuery(id+"F1.opExtrude","CAP_FACE",FACE,{"disambiguationData":[OSD([sQuery(id+"F0.wireOp",EDGE,"E0.bottom"),sQuery(id+"F0.wireOp",EDGE,"E0.top"),sQuery(id+"F0.wireOp",EDGE,"E0.left"),sQuery(id+"F0.wireOp",EDGE,"E0.right")])],"isStart":false}),makeQuery(id+"F4.opExtrude","SWEPT_FACE",FACE,{"disambiguationData":[OSD([sQuery(id+"F2.wireOp",EDGE,"E1.bottom")])]})]}),makeQuery(id+"F6.opExtrude","CAP_FACE",FACE,{"disambiguationData":[OSD([sQuery(id+"F5.wireOp",EDGE,"E2.bottom"),sQuery(id+"F5.wireOp",EDGE,"E2.top"),sQuery(id+"F5.wireOp",EDGE,"E2.left"),sQuery(id+"F5.wireOp",EDGE,"E2.right")])],"isStart":true})]}),makeQuery(id+"F10.opExtrude","SWEPT_FACE",FACE,{"disambiguationData":[OSD([sQuery(id+"F9.wireOp",EDGE,"E4.bottom")])]}),makeQuery(id+"F10.opExtrude","SWEPT_FACE",FACE,{"disambiguationData":[OSD([sQuery(id+"F9.wireOp",EDGE,"E7.bottom")])]})]}),makeQuery(id+"F12.opExtrude","SWEPT_FACE",FACE,{"disambiguationData":[OSD([sQuery(id+"F11.wireOp",EDGE,"E9.bottom")])]})]}),makeQuery(id+"F18.opExtrude","CAP_FACE",FACE,{"disambiguationData":[OSD([sQuery(id+"F17.wireOp",EDGE,"E16.bottom"),sQuery(id+"F17.wireOp",EDGE,"E16.top"),sQuery(id+"F17.wireOp",EDGE,"E16.left"),sQuery(id+"F17.wireOp",EDGE,"E16.right")])],"isStart":true})]}),makeQuery(id+"F20.opExtrude","CAP_FACE",FACE,{"disambiguationData":[OSD([sQuery(id+"F19.wireOp",EDGE,"E17.bottom"),sQuery(id+"F19.wireOp",EDGE,"E17.top"),sQuery(id+"F19.wireOp",EDGE,"E17.left"),sQuery(id+"F19.wireOp",EDGE,"E17.right")])],"isStart":true})]}),makeQuery(id+"F22.opExtrude","CAP_FACE",FACE,{"disambiguationData":[OSD([sQuery(id+"F21.wireOp",EDGE,"E18.bottom"),sQuery(id+"F21.wireOp",EDGE,"E18.top"),sQuery(id+"F21.wireOp",EDGE,"E18.left"),sQuery(id+"F21.wireOp",EDGE,"E18.right")])],"isStart":false})]}),makeQuery(id+"F24.opExtrude","CAP_FACE",FACE,{"disambiguationData":[OSD([sQuery(id+"F23.wireOp",EDGE,"E19.bottom"),sQuery(id+"F23.wireOp",EDGE,"E19.top"),sQuery(id+"F23.wireOp",EDGE,"E19.left"),sQuery(id+"F23.wireOp",EDGE,"E19.right")])],"isStart":true}),makeQuery(id+"F24.opExtrude","CAP_FACE",FACE,{"disambiguationData":[OSD([sQuery(id+"F23.wireOp",EDGE,"E20.bottom"),sQuery(id+"F23.wireOp",EDGE,"E20.top"),sQuery(id+"F23.wireOp",EDGE,"E20.left"),sQuery(id+"F23.wireOp",EDGE,"E20.right")])],"isStart":true})]}),makeQuery(id+"F26.opExtrude","CAP_FACE",FACE,{"disambiguationData":[OSD([sQuery(id+"F25.wireOp",EDGE,"E21.bottom"),sQuery(id+"F25.wireOp",EDGE,"E21.top"),sQuery(id+"F25.wireOp",EDGE,"E21.left"),sQuery(id+"F25.wireOp",EDGE,"E21.right")])],"isStart":true})]}),makeQuery(id+"F28.opExtrude","CAP_FACE",FACE,{"disambiguationData":[OSD([sQuery(id+"F27.wireOp",EDGE,"E22.bottom"),sQuery(id+"F27.wireOp",EDGE,"E22.top"),sQuery(id+"F27.wireOp",EDGE,"E22.left"),sQuery(id+"F27.wireOp",EDGE,"E22.right")])],"isStart":true})]}),makeQuery(id+"F30.opExtrude","CAP_FACE",FACE,{"disambiguationData":[OSD([sQuery(id+"F29.wireOp",EDGE,"E23.bottom"),sQuery(id+"F29.wireOp",EDGE,"E23.top"),sQuery(id+"F29.wireOp",EDGE,"E23.left"),sQuery(id+"F29.wireOp",EDGE,"E23.right")])],"isStart":true})]}),makeQuery(id+"F32.opExtrude","CAP_FACE",FACE,{"disambiguationData":[OSD([sQuery(id+"F31.wireOp",EDGE,"E24.bottom"),sQuery(id+"F31.wireOp",EDGE,"E24.top"),sQuery(id+"F31.wireOp",EDGE,"E24.left"),sQuery(id+"F31.wireOp",EDGE,"E24.right"),sQuery(id+"F31.wireOp",EDGE,"E25.top"),sQuery(id+"F31.wireOp",EDGE,"E25.left"),sQuery(id+"F31.wireOp",EDGE,"E25.right"),sQuery(id+"F31.wireOp",EDGE,"E26.top"),sQuery(id+"F31.wireOp",EDGE,"E26.left"),sQuery(id+"F31.wireOp",EDGE,"E26.right")])],"isStart":true})]}),makeQuery(id+"F34.opExtrude","CAP_FACE",FACE,{"disambiguationData":[OSD([sQuery(id+"F33.wireOp",EDGE,"E27.bottom"),sQuery(id+"F33.wireOp",EDGE,"E27.top"),sQuery(id+"F33.wireOp",EDGE,"E27.left"),sQuery(id+"F33.wireOp",EDGE,"E27.right"),sQuery(id+"F33.wireOp",EDGE,"E28.bottom"),sQuery(id+"F33.wireOp",EDGE,"E28.top"),sQuery(id+"F33.wireOp",EDGE,"E29.bottom"),sQuery(id+"F33.wireOp",EDGE,"E29.top"),sQuery(id+"F33.wireOp",EDGE,"E29.left"),sQuery(id+"F33.wireOp",EDGE,"E29.right"),sQuery(id+"F33.wireOp",EDGE,"E30.bottom"),sQuery(id+"F33.wireOp",EDGE,"E30.top"),sQuery(id+"F33.wireOp",EDGE,"E31.bottom"),sQuery(id+"F33.wireOp",EDGE,"E31.top"),sQuery(id+"F33.wireOp",EDGE,"E31.left"),sQuery(id+"F33.wireOp",EDGE,"E31.right")])],"isStart":true})]}),makeQuery(id+"F36.opExtrude","CAP_FACE",FACE,{"disambiguationData":[OSD([sQuery(id+"F35.wireOp",EDGE,"E32.bottom"),sQuery(id+"F35.wireOp",EDGE,"E32.top"),sQuery(id+"F35.wireOp",EDGE,"E32.left"),sQuery(id+"F35.wireOp",EDGE,"E32.right")])],"isStart":true})]}),makeQuery(id+"F38.opExtrude","CAP_FACE",FACE,{"disambiguationData":[OSD([sQuery(id+"F37.wireOp",EDGE,"E33.bottom"),sQuery(id+"F37.wireOp",EDGE,"E33.top"),sQuery(id+"F37.wireOp",EDGE,"E33.left"),sQuery(id+"F37.wireOp",EDGE,"E33.right")])],"isStart":true})]}),makeQuery(id+"F40.opExtrude","CAP_FACE",FACE,{"disambiguationData":[OSD([sQuery(id+"F39.wireOp",EDGE,"E34.bottom"),sQuery(id+"F39.wireOp",EDGE,"E34.top"),sQuery(id+"F39.wireOp",EDGE,"E34.left"),sQuery(id+"F39.wireOp",EDGE,"E34.right")])],"isStart":true})]}),makeQuery(id+"F42.opExtrude","SWEPT_FACE",FACE,{"disambiguationData":[OSD([sQuery(id+"F41.wireOp",EDGE,"E35.bottom")])]})]}),makeQuery(id+"F44.opExtrude","CAP_FACE",FACE,{"disambiguationData":[OSD([sQuery(id+"F43.wireOp",EDGE,"E37.bottom"),sQuery(id+"F43.wireOp",EDGE,"E37.top"),sQuery(id+"F43.wireOp",EDGE,"E37.left"),sQuery(id+"F43.wireOp",EDGE,"E37.right")])],"isStart":true}),makeQuery(id+"F44.opExtrude","CAP_FACE",FACE,{"disambiguationData":[OSD([sQuery(id+"F43.wireOp",EDGE,"E38.bottom"),sQuery(id+"F43.wireOp",EDGE,"E38.top"),sQuery(id+"F43.wireOp",EDGE,"E38.left"),sQuery(id+"F43.wireOp",EDGE,"E38.right")])],"isStart":true})]}),makeQuery(id+"F46.opExtrude","SWEPT_FACE",FACE,{"disambiguationData":[OSD([sQuery(id+"F45.wireOp",EDGE,"E39.bottom")])]})]}),makeQuery(id+"F48.opExtrude","CAP_FACE",FACE,{"disambiguationData":[OSD([sQuery(id+"F47.wireOp",EDGE,"E41.bottom"),sQuery(id+"F47.wireOp",EDGE,"E41.top"),sQuery(id+"F47.wireOp",EDGE,"E41.left"),sQuery(id+"F47.wireOp",EDGE,"E41.right")])],"isStart":true})]}),makeQuery(id+"F50.opExtrude","SWEPT_FACE",FACE,{"disambiguationData":[OSD([sQuery(id+"F49.wireOp",EDGE,"E42.bottom")])]})]});
            var sketch = newSketch(context, id + "F51", { "sketchPlane" : qUnion([Q0])});
            skLineSegment(sketch, "E44.bottom", {"start": v(-38.07, 425.45) * mm, "end": v(50.83, 425.45) * mm});
            skLineSegment(sketch, "E44.top", {"start": v(-38.07, 444.5) * mm, "end": v(50.83, 444.5) * mm});
            skLineSegment(sketch, "E44.left", {"start": v(-38.07, 425.45) * mm, "end": v(-38.07, 444.5) * mm});
            skLineSegment(sketch, "E44.right", {"start": v(50.83, 425.45) * mm, "end": v(50.83, 444.5) * mm});
            skLineSegment(sketch, "E45.bottom", {"start": v(774.67, 425.45) * mm, "end": v(685.77, 425.45) * mm});
            skLineSegment(sketch, "E45.top", {"start": v(774.67, 444.5) * mm, "end": v(685.77, 444.5) * mm});
            skLineSegment(sketch, "E45.left", {"start": v(774.67, 425.45) * mm, "end": v(774.67, 444.5) * mm});
            skLineSegment(sketch, "E45.right", {"start": v(685.77, 425.45) * mm, "end": v(685.77, 444.5) * mm});
            skSolve(sketch);
        }
        {
            var Q0;
            Q0=makeQuery(id+"F51.imprint","IMPRINT",FACE,{"disambiguationData":[TD([[makeQuery(id+"F51.imprint","IMPRINT",EDGE,{"derivedFrom":sQuery(id+"F51.wireOp",EDGE,"E45.top")}),1.0]])]});
            var Q1;
            Q1=makeQuery(id+"F51.imprint","IMPRINT",FACE,{"disambiguationData":[TD([[makeQuery(id+"F51.imprint","IMPRINT",EDGE,{"derivedFrom":sQuery(id+"F51.wireOp",EDGE,"E44.top")}),-1.0]])]});
            extrude(context, id + "F52", {"entities" : qUnion([Q0, Q1]), "operationType" : NewBodyOperationType.ADD, "oppositeDirection" : true, "depth" : 863.6 * mm, "offsetDistance" : 25.4 * mm});
        }
        {
            var Q0;
            Q0=makeQuery(id+"F52.opExtrude","SWEPT_FACE",FACE,{"disambiguationData":[OSD([sQuery(id+"F51.wireOp",EDGE,"E44.right")])]});
            var sketch = newSketch(context, id + "F53", { "sketchPlane" : qUnion([Q0])});
            skLineSegment(sketch, "E46.bottom", {"start": v(425.45, 406.4) * mm, "end": v(444.47, 406.4) * mm});
            skLineSegment(sketch, "E46.top", {"start": v(425.45, 317.5) * mm, "end": v(444.47, 317.5) * mm});
            skLineSegment(sketch, "E46.left", {"start": v(425.45, 406.4) * mm, "end": v(425.45, 317.5) * mm});
            skLineSegment(sketch, "E46.right", {"start": v(444.47, 406.4) * mm, "end": v(444.47, 317.5) * mm});
            skLineSegment(sketch, "E47.bottom", {"start": v(425.45, 0) * mm, "end": v(444.47, 0) * mm});
            skLineSegment(sketch, "E47.top", {"start": v(425.45, 88.9) * mm, "end": v(444.47, 88.9) * mm});
            skLineSegment(sketch, "E47.left", {"start": v(425.45, 0) * mm, "end": v(425.45, 88.9) * mm});
            skLineSegment(sketch, "E47.right", {"start": v(444.47, 0) * mm, "end": v(444.47, 88.9) * mm});
            skSolve(sketch);
        }
        {
            var Q0;
            Q0=makeQuery(id+"F53.imprint","IMPRINT",FACE,{"disambiguationData":[TD([[makeQuery(id+"F53.imprint","IMPRINT",EDGE,{"derivedFrom":sQuery(id+"F53.wireOp",EDGE,"E47.bottom")}),1.0]])]});
            var Q1;
            Q1=makeQuery(id+"F53.imprint","IMPRINT",FACE,{"disambiguationData":[TD([[makeQuery(id+"F53.imprint","IMPRINT",EDGE,{"derivedFrom":sQuery(id+"F53.wireOp",EDGE,"E46.bottom")}),-1.0]])]});
            extrude(context, id + "F54", {"entities" : qUnion([Q0, Q1]), "operationType" : NewBodyOperationType.ADD, "endBound" : BoundingType.UP_TO_NEXT, "depth" : 25.4 * mm, "offsetDistance" : 25.4 * mm});
        }
        {
            var Q0;
            Q0=makeQuery(id+"F54.boolean.opBoolean","MERGE",FACE,{"derivedFrom":[makeQuery(id+"F52.boolean.opBoolean","MERGE",FACE,{"derivedFrom":[makeQuery(id+"F50.boolean.opBoolean","MERGE",FACE,{"derivedFrom":[makeQuery(id+"F48.boolean.opBoolean","MERGE",FACE,{"derivedFrom":[makeQuery(id+"F46.boolean.opBoolean","MERGE",FACE,{"derivedFrom":[makeQuery(id+"F44.boolean.opBoolean","MERGE",FACE,{"derivedFrom":[makeQuery(id+"F42.boolean.opBoolean","MERGE",FACE,{"derivedFrom":[makeQuery(id+"F40.boolean.opBoolean","MERGE",FACE,{"derivedFrom":[makeQuery(id+"F38.boolean.opBoolean","MERGE",FACE,{"derivedFrom":[makeQuery(id+"F36.boolean.opBoolean","MERGE",FACE,{"derivedFrom":[makeQuery(id+"F34.boolean.opBoolean","MERGE",FACE,{"derivedFrom":[makeQuery(id+"F32.boolean.opBoolean","MERGE",FACE,{"derivedFrom":[makeQuery(id+"F30.boolean.opBoolean","MERGE",FACE,{"derivedFrom":[makeQuery(id+"F28.boolean.opBoolean","MERGE",FACE,{"derivedFrom":[makeQuery(id+"F26.boolean.opBoolean","MERGE",FACE,{"derivedFrom":[makeQuery(id+"F24.boolean.opBoolean","MERGE",FACE,{"derivedFrom":[makeQuery(id+"F22.boolean.opBoolean","MERGE",FACE,{"derivedFrom":[makeQuery(id+"F20.boolean.opBoolean","MERGE",FACE,{"derivedFrom":[makeQuery(id+"F18.boolean.opBoolean","MERGE",FACE,{"derivedFrom":[makeQuery(id+"F12.boolean.opBoolean","MERGE",FACE,{"derivedFrom":[makeQuery(id+"F10.boolean.opBoolean","MERGE",FACE,{"derivedFrom":[makeQuery(id+"F6.boolean.opBoolean","MERGE",FACE,{"derivedFrom":[makeQuery(id+"F4.boolean.opBoolean","MERGE",FACE,{"derivedFrom":[makeQuery(id+"F1.opExtrude","CAP_FACE",FACE,{"disambiguationData":[OSD([sQuery(id+"F0.wireOp",EDGE,"E0.bottom"),sQuery(id+"F0.wireOp",EDGE,"E0.top"),sQuery(id+"F0.wireOp",EDGE,"E0.left"),sQuery(id+"F0.wireOp",EDGE,"E0.right")])],"isStart":false}),makeQuery(id+"F4.opExtrude","SWEPT_FACE",FACE,{"disambiguationData":[OSD([sQuery(id+"F2.wireOp",EDGE,"E1.bottom")])]})]}),makeQuery(id+"F6.opExtrude","CAP_FACE",FACE,{"disambiguationData":[OSD([sQuery(id+"F5.wireOp",EDGE,"E2.bottom"),sQuery(id+"F5.wireOp",EDGE,"E2.top"),sQuery(id+"F5.wireOp",EDGE,"E2.left"),sQuery(id+"F5.wireOp",EDGE,"E2.right")])],"isStart":true})]}),makeQuery(id+"F10.opExtrude","SWEPT_FACE",FACE,{"disambiguationData":[OSD([sQuery(id+"F9.wireOp",EDGE,"E4.bottom")])]}),makeQuery(id+"F10.opExtrude","SWEPT_FACE",FACE,{"disambiguationData":[OSD([sQuery(id+"F9.wireOp",EDGE,"E7.bottom")])]})]}),makeQuery(id+"F12.opExtrude","SWEPT_FACE",FACE,{"disambiguationData":[OSD([sQuery(id+"F11.wireOp",EDGE,"E9.bottom")])]})]}),makeQuery(id+"F18.opExtrude","CAP_FACE",FACE,{"disambiguationData":[OSD([sQuery(id+"F17.wireOp",EDGE,"E16.bottom"),sQuery(id+"F17.wireOp",EDGE,"E16.top"),sQuery(id+"F17.wireOp",EDGE,"E16.left"),sQuery(id+"F17.wireOp",EDGE,"E16.right")])],"isStart":true})]}),makeQuery(id+"F20.opExtrude","CAP_FACE",FACE,{"disambiguationData":[OSD([sQuery(id+"F19.wireOp",EDGE,"E17.bottom"),sQuery(id+"F19.wireOp",EDGE,"E17.top"),sQuery(id+"F19.wireOp",EDGE,"E17.left"),sQuery(id+"F19.wireOp",EDGE,"E17.right")])],"isStart":true})]}),makeQuery(id+"F22.opExtrude","CAP_FACE",FACE,{"disambiguationData":[OSD([sQuery(id+"F21.wireOp",EDGE,"E18.bottom"),sQuery(id+"F21.wireOp",EDGE,"E18.top"),sQuery(id+"F21.wireOp",EDGE,"E18.left"),sQuery(id+"F21.wireOp",EDGE,"E18.right")])],"isStart":false})]}),makeQuery(id+"F24.opExtrude","CAP_FACE",FACE,{"disambiguationData":[OSD([sQuery(id+"F23.wireOp",EDGE,"E19.bottom"),sQuery(id+"F23.wireOp",EDGE,"E19.top"),sQuery(id+"F23.wireOp",EDGE,"E19.left"),sQuery(id+"F23.wireOp",EDGE,"E19.right")])],"isStart":true}),makeQuery(id+"F24.opExtrude","CAP_FACE",FACE,{"disambiguationData":[OSD([sQuery(id+"F23.wireOp",EDGE,"E20.bottom"),sQuery(id+"F23.wireOp",EDGE,"E20.top"),sQuery(id+"F23.wireOp",EDGE,"E20.left"),sQuery(id+"F23.wireOp",EDGE,"E20.right")])],"isStart":true})]}),makeQuery(id+"F26.opExtrude","CAP_FACE",FACE,{"disambiguationData":[OSD([sQuery(id+"F25.wireOp",EDGE,"E21.bottom"),sQuery(id+"F25.wireOp",EDGE,"E21.top"),sQuery(id+"F25.wireOp",EDGE,"E21.left"),sQuery(id+"F25.wireOp",EDGE,"E21.right")])],"isStart":true})]}),makeQuery(id+"F28.opExtrude","CAP_FACE",FACE,{"disambiguationData":[OSD([sQuery(id+"F27.wireOp",EDGE,"E22.bottom"),sQuery(id+"F27.wireOp",EDGE,"E22.top"),sQuery(id+"F27.wireOp",EDGE,"E22.left"),sQuery(id+"F27.wireOp",EDGE,"E22.right")])],"isStart":true})]}),makeQuery(id+"F30.opExtrude","CAP_FACE",FACE,{"disambiguationData":[OSD([sQuery(id+"F29.wireOp",EDGE,"E23.bottom"),sQuery(id+"F29.wireOp",EDGE,"E23.top"),sQuery(id+"F29.wireOp",EDGE,"E23.left"),sQuery(id+"F29.wireOp",EDGE,"E23.right")])],"isStart":true})]}),makeQuery(id+"F32.opExtrude","CAP_FACE",FACE,{"disambiguationData":[OSD([sQuery(id+"F31.wireOp",EDGE,"E24.bottom"),sQuery(id+"F31.wireOp",EDGE,"E24.top"),sQuery(id+"F31.wireOp",EDGE,"E24.left"),sQuery(id+"F31.wireOp",EDGE,"E24.right"),sQuery(id+"F31.wireOp",EDGE,"E25.top"),sQuery(id+"F31.wireOp",EDGE,"E25.left"),sQuery(id+"F31.wireOp",EDGE,"E25.right"),sQuery(id+"F31.wireOp",EDGE,"E26.top"),sQuery(id+"F31.wireOp",EDGE,"E26.left"),sQuery(id+"F31.wireOp",EDGE,"E26.right")])],"isStart":true})]}),makeQuery(id+"F34.opExtrude","CAP_FACE",FACE,{"disambiguationData":[OSD([sQuery(id+"F33.wireOp",EDGE,"E27.bottom"),sQuery(id+"F33.wireOp",EDGE,"E27.top"),sQuery(id+"F33.wireOp",EDGE,"E27.left"),sQuery(id+"F33.wireOp",EDGE,"E27.right"),sQuery(id+"F33.wireOp",EDGE,"E28.bottom"),sQuery(id+"F33.wireOp",EDGE,"E28.top"),sQuery(id+"F33.wireOp",EDGE,"E29.bottom"),sQuery(id+"F33.wireOp",EDGE,"E29.top"),sQuery(id+"F33.wireOp",EDGE,"E29.left"),sQuery(id+"F33.wireOp",EDGE,"E29.right"),sQuery(id+"F33.wireOp",EDGE,"E30.bottom"),sQuery(id+"F33.wireOp",EDGE,"E30.top"),sQuery(id+"F33.wireOp",EDGE,"E31.bottom"),sQuery(id+"F33.wireOp",EDGE,"E31.top"),sQuery(id+"F33.wireOp",EDGE,"E31.left"),sQuery(id+"F33.wireOp",EDGE,"E31.right")])],"isStart":true})]}),makeQuery(id+"F36.opExtrude","CAP_FACE",FACE,{"disambiguationData":[OSD([sQuery(id+"F35.wireOp",EDGE,"E32.bottom"),sQuery(id+"F35.wireOp",EDGE,"E32.top"),sQuery(id+"F35.wireOp",EDGE,"E32.left"),sQuery(id+"F35.wireOp",EDGE,"E32.right")])],"isStart":true})]}),makeQuery(id+"F38.opExtrude","CAP_FACE",FACE,{"disambiguationData":[OSD([sQuery(id+"F37.wireOp",EDGE,"E33.bottom"),sQuery(id+"F37.wireOp",EDGE,"E33.top"),sQuery(id+"F37.wireOp",EDGE,"E33.left"),sQuery(id+"F37.wireOp",EDGE,"E33.right")])],"isStart":true})]}),makeQuery(id+"F40.opExtrude","CAP_FACE",FACE,{"disambiguationData":[OSD([sQuery(id+"F39.wireOp",EDGE,"E34.bottom"),sQuery(id+"F39.wireOp",EDGE,"E34.top"),sQuery(id+"F39.wireOp",EDGE,"E34.left"),sQuery(id+"F39.wireOp",EDGE,"E34.right")])],"isStart":true})]}),makeQuery(id+"F42.opExtrude","SWEPT_FACE",FACE,{"disambiguationData":[OSD([sQuery(id+"F41.wireOp",EDGE,"E35.bottom")])]})]}),makeQuery(id+"F44.opExtrude","CAP_FACE",FACE,{"disambiguationData":[OSD([sQuery(id+"F43.wireOp",EDGE,"E37.bottom"),sQuery(id+"F43.wireOp",EDGE,"E37.top"),sQuery(id+"F43.wireOp",EDGE,"E37.left"),sQuery(id+"F43.wireOp",EDGE,"E37.right")])],"isStart":true}),makeQuery(id+"F44.opExtrude","CAP_FACE",FACE,{"disambiguationData":[OSD([sQuery(id+"F43.wireOp",EDGE,"E38.bottom"),sQuery(id+"F43.wireOp",EDGE,"E38.top"),sQuery(id+"F43.wireOp",EDGE,"E38.left"),sQuery(id+"F43.wireOp",EDGE,"E38.right")])],"isStart":true})]}),makeQuery(id+"F46.opExtrude","SWEPT_FACE",FACE,{"disambiguationData":[OSD([sQuery(id+"F45.wireOp",EDGE,"E39.bottom")])]})]}),makeQuery(id+"F48.opExtrude","CAP_FACE",FACE,{"disambiguationData":[OSD([sQuery(id+"F47.wireOp",EDGE,"E41.bottom"),sQuery(id+"F47.wireOp",EDGE,"E41.top"),sQuery(id+"F47.wireOp",EDGE,"E41.left"),sQuery(id+"F47.wireOp",EDGE,"E41.right")])],"isStart":true})]}),makeQuery(id+"F50.opExtrude","SWEPT_FACE",FACE,{"disambiguationData":[OSD([sQuery(id+"F49.wireOp",EDGE,"E42.bottom")])]})]}),makeQuery(id+"F52.opExtrude","CAP_FACE",FACE,{"disambiguationData":[OSD([sQuery(id+"F51.wireOp",EDGE,"E44.bottom"),sQuery(id+"F51.wireOp",EDGE,"E44.top"),sQuery(id+"F51.wireOp",EDGE,"E44.left"),sQuery(id+"F51.wireOp",EDGE,"E44.right")])],"isStart":true}),makeQuery(id+"F52.opExtrude","CAP_FACE",FACE,{"disambiguationData":[OSD([sQuery(id+"F51.wireOp",EDGE,"E45.bottom"),sQuery(id+"F51.wireOp",EDGE,"E45.top"),sQuery(id+"F51.wireOp",EDGE,"E45.left"),sQuery(id+"F51.wireOp",EDGE,"E45.right")])],"isStart":true})]}),makeQuery(id+"F54.opExtrude","SWEPT_FACE",FACE,{"disambiguationData":[OSD([sQuery(id+"F53.wireOp",EDGE,"E46.bottom")])]})]});
            var sketch = newSketch(context, id + "F55", { "sketchPlane" : qUnion([Q0])});
            skLineSegment(sketch, "E48.bottom", {"start": v(787.43, 0) * mm, "end": v(-50.77, 0) * mm});
            skLineSegment(sketch, "E48.top", {"start": v(787.43, -88.9) * mm, "end": v(-50.77, -88.9) * mm});
            skLineSegment(sketch, "E48.left", {"start": v(787.43, 0) * mm, "end": v(787.43, -88.9) * mm});
            skLineSegment(sketch, "E48.right", {"start": v(-50.77, 0) * mm, "end": v(-50.77, -88.9) * mm});
            skSolve(sketch);
        }
        {
            var Q0;
            Q0=makeQuery(id+"F55.imprint","IMPRINT",FACE,{"disambiguationData":[TD([[makeQuery(id+"F55.imprint","IMPRINT",EDGE,{"derivedFrom":sQuery(id+"F55.wireOp",EDGE,"E48.top")}),-1.0]])]});
            var Q1;
            {var subQ1=sQuery(id+"F23.wireOp",EDGE,"E20.right");Q1=makeQuery(id+"F55.imprint","IMPRINT",FACE,{"disambiguationData":[TD([[makeQuery(id+"F55.imprint","IMPRINT",EDGE,{"derivedFrom":makeQuery(id+"F24.opExtrude","CAP_EDGE",EDGE,{"disambiguationData":[OSD([subQ1])],"isStart":true})}),-1.0]])]});}
            var Q2;
            {var subQ18=sQuery(id+"F19.wireOp",EDGE,"E17.top");Q2=makeQuery(id+"F55.imprint","IMPRINT",FACE,{"disambiguationData":[TD([[makeQuery(id+"F55.imprint","IMPRINT",EDGE,{"derivedFrom":makeQuery(id+"F20.opExtrude","CAP_EDGE",EDGE,{"disambiguationData":[OSD([subQ18])],"isStart":true})}),1.0]])]});}
            var Q3;
            {var subQ22=sQuery(id+"F23.wireOp",EDGE,"E19.right");Q3=makeQuery(id+"F55.imprint","IMPRINT",FACE,{"disambiguationData":[TD([[makeQuery(id+"F55.imprint","IMPRINT",EDGE,{"derivedFrom":makeQuery(id+"F24.opExtrude","CAP_EDGE",EDGE,{"disambiguationData":[OSD([subQ22])],"isStart":true})}),1.0]])]});}
            extrude(context, id + "F56", {"entities" : qUnion([Q0, Q1, Q2, Q3]), "operationType" : NewBodyOperationType.ADD, "depth" : 19.05 * mm, "offsetDistance" : 25.4 * mm});
        }
        {
            var Q0;
            {var subQ1=sQuery(id+"F5.wireOp",EDGE,"E2.bottom");var subQ2=makeQuery(id+"F6.opExtrude","SWEPT_FACE",FACE,{"disambiguationData":[OSD([subQ1])]});var subQ3=makeQuery(id+"F4.opExtrude","SWEPT_FACE",FACE,{"disambiguationData":[OSD([sQuery(id+"F2.wireOp",EDGE,"E1.right")])]});var subQ5=sQuery(id+"F0.wireOp",EDGE,"E0.bottom");var subQ6=makeQuery(id+"F1.opExtrude","SWEPT_FACE",FACE,{"disambiguationData":[OSD([subQ5])]});var subQ7=makeQuery(id+"F8.opExtrude","SWEPT_FACE",FACE,{"disambiguationData":[OSD([sQuery(id+"F7.wireOp",EDGE,"E3.right")])]});Q0=makeQuery(id+"F56.boolean.opBoolean","MERGE",FACE,{"derivedFrom":[makeQuery(id+"F10.boolean.opBoolean","SPLIT",FACE,{"disambiguationData":[TD([makeQuery(id+"F4.opExtrude","SWEPT_FACE",FACE,{"disambiguationData":[OSD([sQuery(id+"F2.wireOp",EDGE,"E1.bottom")])]})])],"derivedFrom":makeQuery(id+"F8.boolean.opBoolean","MERGE",FACE,{"derivedFrom":[makeQuery(id+"F6.boolean.opBoolean","MERGE",FACE,{"derivedFrom":[makeQuery(id+"F4.boolean.opBoolean","MERGE",FACE,{"derivedFrom":[subQ6,subQ3]}),subQ2]}),subQ7]})}),makeQuery(id+"F56.opExtrude","SWEPT_FACE",FACE,{"disambiguationData":[OSD([sQuery(id+"F55.wireOp",EDGE,"E48.bottom")])]})]});}
            var sketch = newSketch(context, id + "F57", { "sketchPlane" : qUnion([Q0])});
            skLineSegment(sketch, "E49.bottom", {"start": v(-787.43, 406.4) * mm, "end": v(-698.53, 406.4) * mm});
            skLineSegment(sketch, "E49.top", {"start": v(-787.43, 425.45) * mm, "end": v(-698.53, 425.45) * mm});
            skLineSegment(sketch, "E49.left", {"start": v(-787.43, 406.4) * mm, "end": v(-787.43, 425.45) * mm});
            skLineSegment(sketch, "E49.right", {"start": v(-698.53, 406.4) * mm, "end": v(-698.53, 425.45) * mm});
            skLineSegment(sketch, "E50.bottom", {"start": v(-38.1, 406.4) * mm, "end": v(50.77, 406.4) * mm});
            skLineSegment(sketch, "E50.top", {"start": v(-38.1, 425.45) * mm, "end": v(50.77, 425.45) * mm});
            skLineSegment(sketch, "E50.left", {"start": v(-38.1, 406.4) * mm, "end": v(-38.1, 425.45) * mm});
            skLineSegment(sketch, "E50.right", {"start": v(50.77, 406.4) * mm, "end": v(50.77, 425.45) * mm});
            skSolve(sketch);
        }
        {
            var Q0;
            Q0=makeQuery(id+"F57.imprint","IMPRINT",FACE,{"disambiguationData":[TD([[makeQuery(id+"F57.imprint","IMPRINT",EDGE,{"derivedFrom":sQuery(id+"F57.wireOp",EDGE,"E49.top")}),-1.0]])]});
            var Q1;
            Q1=makeQuery(id+"F57.imprint","IMPRINT",FACE,{"disambiguationData":[TD([[makeQuery(id+"F57.imprint","IMPRINT",EDGE,{"derivedFrom":sQuery(id+"F57.wireOp",EDGE,"E50.top")}),-1.0]])]});
            extrude(context, id + "F58", {"entities" : qUnion([Q0, Q1]), "operationType" : NewBodyOperationType.ADD, "depth" : 368.3 * mm, "offsetDistance" : 25.4 * mm});
        }
        {
            var Q0;
            Q0=makeQuery(id+"F58.boolean.opBoolean","MERGE",FACE,{"derivedFrom":[makeQuery(id+"F56.opExtrude","CAP_FACE",FACE,{"disambiguationData":[OSD([sQuery(id+"F17.wireOp",EDGE,"E16.left"),sQuery(id+"F17.wireOp",EDGE,"E16.right"),sQuery(id+"F19.wireOp",EDGE,"E17.top"),sQuery(id+"F21.wireOp",EDGE,"E18.top"),sQuery(id+"F23.wireOp",EDGE,"E19.top"),sQuery(id+"F23.wireOp",EDGE,"E19.left"),sQuery(id+"F23.wireOp",EDGE,"E20.left"),sQuery(id+"F39.wireOp",EDGE,"E34.bottom"),sQuery(id+"F39.wireOp",EDGE,"E34.right"),sQuery(id+"F55.wireOp",EDGE,"E48.bottom"),sQuery(id+"F55.wireOp",EDGE,"E48.top"),sQuery(id+"F55.wireOp",EDGE,"E48.left"),sQuery(id+"F55.wireOp",EDGE,"E48.right")])],"isStart":false}),makeQuery(id+"F58.opExtrude","SWEPT_FACE",FACE,{"disambiguationData":[OSD([sQuery(id+"F57.wireOp",EDGE,"E49.top")])]}),makeQuery(id+"F58.opExtrude","SWEPT_FACE",FACE,{"disambiguationData":[OSD([sQuery(id+"F57.wireOp",EDGE,"E50.top")])]})]});
            var sketch = newSketch(context, id + "F59", { "sketchPlane" : qUnion([Q0])});
            skLineSegment(sketch, "E51.bottom", {"start": v(-50.77, 368.3) * mm, "end": v(787.43, 368.3) * mm});
            skLineSegment(sketch, "E51.top", {"start": v(-50.77, 457.2) * mm, "end": v(787.43, 457.2) * mm});
            skLineSegment(sketch, "E51.left", {"start": v(-50.77, 368.3) * mm, "end": v(-50.77, 457.2) * mm});
            skLineSegment(sketch, "E51.right", {"start": v(787.43, 368.3) * mm, "end": v(787.43, 457.2) * mm});
            skSolve(sketch);
        }
        {
            var Q0;
            Q0=makeQuery(id+"F59.imprint","IMPRINT",FACE,{"disambiguationData":[TD([[makeQuery(id+"F59.imprint","IMPRINT",EDGE,{"derivedFrom":sQuery(id+"F59.wireOp",EDGE,"E51.top")}),-1.0]])]});
            extrude(context, id + "F60", {"entities" : qUnion([Q0]), "operationType" : NewBodyOperationType.ADD, "oppositeDirection" : true, "depth" : 19.05 * mm, "offsetDistance" : 25.4 * mm});
        }
    });
